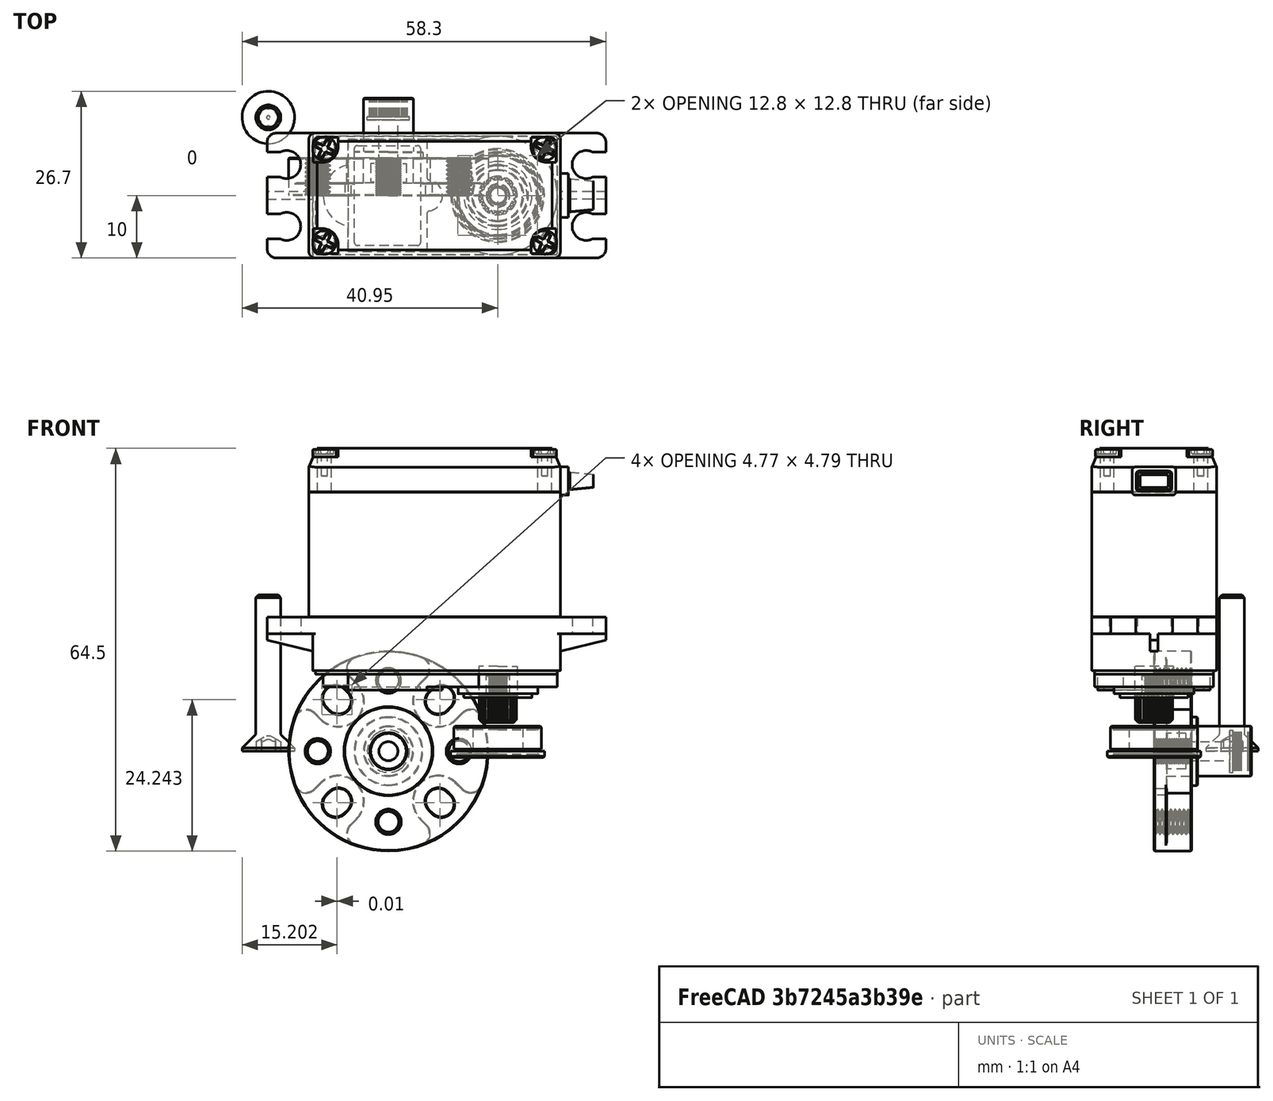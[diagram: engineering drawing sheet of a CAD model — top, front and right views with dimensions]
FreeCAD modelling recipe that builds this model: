
FCSTD DOCUMENT  (FreeCAD 1.1R39747 (Git))
Label: assembly
License: All rights reserved
LicenseURL: https://en.wikipedia.org/wiki/All_rights_reserved
objects: App::Link×11, Part::Feature×3, App::Part×2, App::Point×2, Part::FeaturePython×1, TechDraw::DrawSVGTemplate×1, App::DocumentObjectGroup×1, TechDraw::DrawProjGroupItem×1, TechDraw::DrawPage×1
note: 4 computed .brp shape members not serialized (recipe doc carries the construction recipe); baked Part::Feature solids carry a one-line shape summary decoded from their .brp
EXTERNAL_REF file=claw-base.FCStd obj=Body
EXTERNAL_REF file=claw-back.FCStd obj=Pad
EXTERNAL_REF file=claw-back.FCStd obj=Pad001
EXTERNAL_REF file=claw-back.FCStd obj=Body
EXTERNAL_REF file=variables.FCStd obj=Spreadsheet
EXTERNAL_REF file=claw-pinchers.FCStd obj=InvoluteGear
EXTERNAL_REF file=claw-pinchers.FCStd obj=Body
EXTERNAL_REF file=claw-pinchers.FCStd obj=Body001
EXTERNAL_REF file=DS3225Pro.FCStd obj=DS3225_Pro_Servo_25Kg_4_8_6_8V_H
EXTERNAL_REF file=claw-base.FCStd obj=Sketch001

FEATURE [App::Link] Link  label="Claw Base Body"
  LinkedObject = -> <external claw-base.FCStd>#Body
FEATURE [App::Link] Link001  label="Claw Back Body"
  LinkPlacement = pos=(0,0,-27) rot=(0,0,1;0rad)
  LinkedObject = -> <external claw-back.FCStd>#Body
  Placement = pos=(0,0,-27) rot=(0,0,1;0rad)
  expr: .LinkPlacement.Base.z = -(claw_back#Pad001.Length + claw_back#Pad.Length)
FEATURE [Part::Feature] Part__Feature  label="1611-0514-0008"
  Placement = pos=(17.5,0,4) rot=(1,0,0;-1.5708rad)
  shape: bbox 15 x 15 x 5 mm, 86 faces, 3 solids (baked)
  expr: .Placement.Base.x = variables#Spreadsheet.claw_pincher_c2c / 2
FEATURE [Part::Feature] Part__Feature001  label="1910-0025-0816"
  shape: bbox 32 x 15.92 x 32 mm, 420 faces (baked)
FEATURE [App::Part] _910_0025_0816  label="1910-0025-0817"
  Group = -> [Part__Feature001]
  Origin = -> Origin001
  Placement = pos=(17.5,0,-8) rot=(1,0,0;1.5708rad)
  expr: .Placement.Base.x = variables#Spreadsheet.claw_pincher_c2c / 2
FEATURE [Part::Feature] Part__Feature003  label="2000-0025-0002"
  Placement = pos=(7.7,2.3e-15,10.3) rot=(0,-1,0;3.14159rad)
  shape: bbox 54.3 x 20.57 x 43.9 mm, 516 faces, 2 solids (baked)
  expr: Visibility = variables#Spreadsheet.gobilda_servo_visible
FEATURE [App::Link] Link002  label="1611-0514-0009"
  LinkPlacement = pos=(-17.5,0,4) rot=(1,0,0;-1.5708rad)
  LinkedObject = -> Part__Feature
  Placement = pos=(-17.5,0,4) rot=(1,0,0;-1.5708rad)
  expr: .Placement.Base.x = -<<1611-0514-0008>>.Placement.Base.x
  expr: .Placement.Base.z = <<1611-0514-0008>>.Placement.Base.z
FEATURE [App::Link] Link003  label="1611-0514-0010"
  LinkPlacement = pos=(-17.5,0,-26) rot=(1,0,0;1.5708rad)
  LinkedObject = -> Part__Feature
  Placement = pos=(-17.5,0,-26) rot=(1,0,0;1.5708rad)
  expr: .Placement.Base.x = -<<1611-0514-0011>>.Placement.Base.x
  expr: .Placement.Base.z = <<1611-0514-0011>>.Placement.Base.z
FEATURE [App::Link] Link004  label="1611-0514-0011"
  LinkPlacement = pos=(17.5,0,-26) rot=(1,0,0;1.5708rad)
  LinkedObject = -> Link002
  Placement = pos=(17.5,0,-26) rot=(1,0,0;1.5708rad)
  expr: .Placement.Base.x = <<1611-0514-0008>>.Placement.Base.x
  expr: .Placement.Base.z = Link001.Placement.Base.z + claw_back#Pad.Length - 4 mm
FEATURE [App::Link] Link005  label="Claw Pincher Powered"
  LinkPlacement = pos=(17.5,0,-16.4) rot=(0,0,1;3.14159rad)
  LinkedObject = -> <external claw-pinchers.FCStd>#Body
  Placement = pos=(17.5,0,-16.4) rot=(0,0,1;3.14159rad)
  expr: .Placement.Base.x = variables#Spreadsheet.claw_pincher_c2c / 2
  expr: .Placement.Base.z = -claw_pinchers#InvoluteGear.height - 8 mm
FEATURE [App::Link] Link006  label="Claw Pincher Passive"
  LinkPlacement = pos=(17.5,0,-16.4) rot=(0,0,1;3.14159rad)
  LinkedObject = -> <external claw-pinchers.FCStd>#Body001
  Placement = pos=(17.5,0,-16.4) rot=(0,0,1;3.14159rad)
  expr: .Placement.Base.x = <<Claw Pincher Powered>>.Placement.Base.x
  expr: .Placement.Base.z = <<Claw Pincher Powered>>.Placement.Base.z
FEATURE [App::Link] Link007  label="DS3225 Pro Servo 25Kg 4.8-6.8V H"
  LinkPlacement = pos=(8,-6.6,29.88) rot=(0,-1,0;3.14159rad)
  LinkedObject = -> <external DS3225Pro.FCStd>#DS3225_Pro_Servo_25Kg_4_8_6_8V_H
  Placement = pos=(8,-6.6,29.88) rot=(0,-1,0;3.14159rad)
  expr: Visibility = variables#Spreadsheet.dsservo_visible
FEATURE [Part::FeaturePython] Screw  label="M4x25-Screw"  # WARN: FeaturePython — macro-defined, semantics opaque (R4)
  Diameter = 5
  Invert = false
  LeftHanded = false
  Length = 6
  LengthCustom = 25
  MatchOuter = false
  OffsetAngle = 0
  Placement = pos=(-19.25,12.5,0) rot=(1,0,0;3.14159rad)
  Thread = false
  Type = 54
  expr: .Placement.Base.x = -claw_base#Sketch001.Constraints.structure_hole_x
  expr: .Placement.Base.y = claw_base#Sketch001.Constraints.structure_holes_y
FEATURE [TechDraw::DrawSVGTemplate] Template
  Height = 210
  Orientation = 1
  Template = <path>
  Width = 297
FEATURE [App::Link] Link008  label="M4x8-Screw001"
  LinkPlacement = pos=(-19.25,-12.5,0) rot=(1,0,0;3.14159rad)
  LinkedObject = -> Screw
  Placement = pos=(-19.25,-12.5,0) rot=(1,0,0;3.14159rad)
  expr: .Placement.Base.x = -claw_base#Sketch001.Constraints.structure_hole_x
  expr: .Placement.Base.y = -claw_base#Sketch001.Constraints.structure_holes_y
FEATURE [App::Link] Link009  label="M4x8-Screw002"
  LinkPlacement = pos=(34.25,-12.5,0) rot=(1,0,0;3.14159rad)
  LinkedObject = -> Link008
  Placement = pos=(34.25,-12.5,0) rot=(1,0,0;3.14159rad)
  expr: .Placement.Base.x = -claw_base#Sketch001.Constraints.structure_hole_x + claw_base#Sketch001.Constraints.structure_holes_c2c
  expr: .Placement.Base.y = -claw_base#Sketch001.Constraints.structure_holes_y
FEATURE [App::Link] Link010  label="M4x8-Screw003"
  LinkPlacement = pos=(34.25,12.5,0) rot=(1,0,0;3.14159rad)
  LinkedObject = -> Link009
  Placement = pos=(34.25,12.5,0) rot=(1,0,0;3.14159rad)
  expr: .Placement.Base.x = -claw_base#Sketch001.Constraints.structure_hole_x + claw_base#Sketch001.Constraints.structure_holes_c2c
  expr: .Placement.Base.y = claw_base#Sketch001.Constraints.structure_holes_y
FEATURE [App::Point] Origin002  label="Origin"
  Role = Origin
FEATURE [App::Point] Origin003  label="Origin"
  Role = Origin
FEATURE [App::DocumentObjectGroup] Group  label="AssemblyGroup"
  Group = -> [Link,Link001,Part__Feature,_910_0025_0816,Part__Feature003,Link002,Link004,Link003,Link005,Link006,Link007,Screw,Link008,Link009,Link010]
FEATURE [App::Part] Part  label="Assembly"
  Group = -> [Group,Link,Link001,Part__Feature,_910_0025_0816,Part__Feature003,Link002,Link004,Link003,Link005,Link006,Link007,Screw,Link008,Link009,Link010]
  Origin = -> Origin
  Placement = pos=(0,0,34) rot=(0,0,1;0rad)
FEATURE [TechDraw::DrawProjGroupItem] View
  CoarseView = false
  Direction = (0,0,1)
  Focus = 100
  HardHidden = false
  IsoCount = 0
  IsoHidden = false
  IsoVisible = false
  LockPosition = false
  Perspective = false
  Rotation = 0
  RotationVector = (1,0,0)
  ScaleType = 0
  ScrubCount = 1
  SeamHidden = false
  SeamVisible = false
  SmoothHidden = false
  SmoothVisible = true
  Source = -> [Part]
  Type = 0
  X = 88.6183
  XDirection = (1,0,0)
  Y = 125.531
FEATURE [TechDraw::DrawPage] Page
  KeepUpdated = false
  NextBalloonIndex = 1
  ProjectionType = 0
  Template = -> Template
  Views = -> [View]
note: 1 file-system path scrubbed to <path> (originals preserved in the JSON sidecar)

RESOLVED EXTERNAL PARTS (link-assembly join: the EXTERNAL_REF files above that resolve inside this repo's crawl, each included once):
---- part claw-back.FCStd = doc fcstd_3221efbdef80 ----
FCSTD DOCUMENT  (FreeCAD 1.1R39747 (Git))
Label: claw-back
License: All rights reserved
LicenseURL: https://en.wikipedia.org/wiki/All_rights_reserved
objects: Sketcher::SketchObject×12, PartDesign::Pad×6, PartDesign::Pocket×5, App::Point×2, PartDesign::Hole×1, Part::LocalCoordinateSystem×1, PartDesign::AdditivePipe×1, PartDesign::Body×1
note: 64 computed .brp shape members not serialized (recipe doc carries the construction recipe); baked Part::Feature solids carry a one-line shape summary decoded from their .brp
EXTERNAL_REF file=variables.FCStd obj=Spreadsheet

FEATURE [Sketcher::SketchObject] Sketch
  ArcFitTolerance = 1e-06
  AttachmentSupport = -> [XY_Plane]
  ExternalTypes = [0]
  FullyConstrained = false
  MakeInternals = false
  MapMode = 5
  expr: Constraints[1] = <<variables>>#Spreadsheet.claw_pincher_c2c
  expr: Constraints[30] = <<variables>>#Spreadsheet.claw_back_outer_spacer_holes_wing_angle
  expr: Constraints[33] = <<variables>>#Spreadsheet.claw_back_spacer_diameter / 2
  expr: Constraints[50] = <<variables>>#Spreadsheet.claw_back_outer_spacer_holes_wing_angle
  expr: Constraints[53] = variables#Spreadsheet.distance_bearing_holes_to_end
  sketch-geometry (27):
    g0: LineSegment [constr] StartX=-17.5 StartY=1.14452e-11 StartZ=0 EndX=17.5 EndY=1.14452e-11 EndZ=0
    g1: Circle CenterX=-17.5 CenterY=1.14452e-11 CenterZ=0 NormalX=0 NormalY=0 NormalZ=1 AngleXU=0 Radius=7
    g2: Circle CenterX=17.5 CenterY=1.14452e-11 CenterZ=0 NormalX=0 NormalY=0 NormalZ=1 AngleXU=0 Radius=7
    g3: LineSegment StartX=-27.5 StartY=26.7321 StartZ=0 EndX=-24.5 EndY=28.4641 EndZ=0
    g4: LineSegment StartX=-22.5 StartY=29 StartZ=0 EndX=22.5 EndY=29 EndZ=0
    g5: LineSegment StartX=24.5 StartY=28.4641 StartZ=0 EndX=27.5 EndY=26.7321 EndZ=0
    g6: GeomPoint X=0 Y=29 Z=0
    g7: LineSegment [constr] StartX=-22.5 StartY=25 StartZ=0 EndX=22.5 EndY=25 EndZ=0
    g8: GeomPoint [constr] X=1.28886e-11 Y=25 Z=0
    g9: Circle CenterX=-22.5 CenterY=25 CenterZ=0 NormalX=0 NormalY=0 NormalZ=1 AngleXU=0 Radius=2.25
    g10: Circle CenterX=22.5 CenterY=25 CenterZ=0 NormalX=0 NormalY=0 NormalZ=1 AngleXU=0 Radius=2.25
    g11: Circle [constr] CenterX=-22.5 CenterY=25 CenterZ=0 NormalX=0 NormalY=0 NormalZ=1 AngleXU=0 Radius=4
    g12: Circle [constr] CenterX=22.5 CenterY=25 CenterZ=0 NormalX=0 NormalY=0 NormalZ=1 AngleXU=0 Radius=4
    g13: ArcOfCircle CenterX=22.5 CenterY=25 CenterZ=0 NormalX=0 NormalY=0 NormalZ=1 AngleXU=0 Radius=4 StartAngle=1.0472 EndAngle=1.5708
    g14: ArcOfCircle CenterX=-22.5 CenterY=25 CenterZ=0 NormalX=0 NormalY=0 NormalZ=1 AngleXU=0 Radius=4 StartAngle=1.5708 EndAngle=2.0944
    g15: LineSegment StartX=25 StartY=-16 StartZ=0 EndX=-25 EndY=-16 EndZ=0
    g16: LineSegment StartX=-30 StartY=22.4019 StartZ=0 EndX=-30 EndY=-11 EndZ=0
    g17: ArcOfCircle CenterX=-25 CenterY=-11 CenterZ=0 NormalX=0 NormalY=0 NormalZ=1 AngleXU=0 Radius=5 StartAngle=3.14159 EndAngle=4.71239
    g18: GeomPoint [constr] X=-30 Y=-16 Z=0
    g19: ArcOfCircle CenterX=-25 CenterY=22.4019 CenterZ=0 NormalX=0 NormalY=0 NormalZ=1 AngleXU=0 Radius=5 StartAngle=2.0944 EndAngle=3.14159
    g20: GeomPoint [constr] X=-30 Y=25.2887 Z=0
    g21: ArcOfCircle CenterX=25 CenterY=-11 CenterZ=0 NormalX=0 NormalY=0 NormalZ=1 AngleXU=0 Radius=5 StartAngle=4.71239 EndAngle=6.28319
    g22: GeomPoint [constr] X=30 Y=-16 Z=0
    g23: ArcOfCircle CenterX=25 CenterY=22.4019 CenterZ=0 NormalX=0 NormalY=0 NormalZ=1 AngleXU=0 Radius=5 StartAngle=3.1057e-12 EndAngle=1.0472
    g24: GeomPoint [constr] X=30.2347 Y=25.1532 Z=0
    g25: GeomPoint [constr] X=0 Y=6 Z=0
    g26: LineSegment StartX=30 StartY=22.4019 StartZ=0 EndX=30 EndY=-11 EndZ=0
  constraints (61):
    c: Horizontal(g0)
    c: DistanceX(g0,g0) = 35
    c: Symmetric(g0,g0,g-1)
    c: Diameter(g1) = 14
    c: Coincident(g1,g0)
    c: Coincident(g2,g0)
    c: Equal(g2,g1)
    c: Horizontal(g4)
    c: PointOnObject(g6,g-2)
    c: Horizontal(g7)
    c: DistanceX(g7,g7) = 45
    c: Distance(g0,g7) = 25
    c: Symmetric(g7,g7,g8)
    c: PointOnObject(g8,g-2)
    c: Coincident(g10,g7)
    c: Equal(g9,g10)
    c: Tangent(g4,g11) = 1.5708
    c: Tangent(g3,g11) = 1.5708
    c: Coincident(g12,g7)
    c: Equal(g12,g11)
    c: Equal(g13,g12)
    c: Tangent(g4,g13) = 1.5708
    c: PointOnObject(g6,g4)
    c: Coincident(g5,g13)
    c: Tangent(g5,g12) = 1.5708
    c: Coincident(g14,g3)
    c: Coincident(g14,g4)
    c: Equal(g14,g11)
    c: Diameter(g9) = 4.5
    c: Vertical(g16)
    c: Angle(g3,g7) = 2.61799
    c: Coincident(g9,g14)
    c: Coincident(g7,g11)
    c: Radius(g14) = 4
    c: Horizontal(g15)
    c: PointOnObject(g18,g15)
    c: PointOnObject(g18,g16)
    c: Tangent(g15,g17) = 1.5708
    c: Tangent(g16,g17) = -1.5708
    c: PointOnObject(g20,g3)
    c: PointOnObject(g20,g16)
    c: Tangent(g3,g19) = 1.5708
    c: Tangent(g16,g19) = -1.5708
    c: Radius(g17) = 5
    c: Equal(g19,g17)
    c: Tangent(g26,g21) = 1.5708
    c: Equal(g21,g17)
    c: PointOnObject(g24,g5)
    c: Tangent(g5,g23) = 1.5708
    c: Equal(g23,g21)
    c: Angle(g7,g5) = 2.61799
    c: Horizontal(g22,g15)
    c: Equal(g3,g5)
    c: Distance(g15,g0) = 16
    c: Tangent(g21,g15) = 1.5708
    c: PointOnObject(g25,g-2)
    c: Distance(g25,g0) = 6
    c: Vertical(g26)
    c: PointOnObject(g22,g26)
    c: Tangent(g26,g23) = 1.5708
    c: Distance(g26,g16) = 60
FEATURE [PartDesign::Pad] Pad
  Direction = (0,0,1)
  Length = 5
  Length2 = 10
  Profile = -> Sketch
  ReferenceAxis = -> Sketch [N_Axis]
  Refine = true
  Suppressed = false
  Type = 0
FEATURE [Sketcher::SketchObject] Sketch001
  ArcFitTolerance = 1e-06
  AttachmentSupport = -> [Pad]
  ExternalGeometry = -> [Pad]
  ExternalTypes = [0]
  FullyConstrained = true
  MakeInternals = false
  MapMode = 5
  Placement = pos=(0,0,5) rot=(0,0,1;0rad)
  expr: Constraints[12] = <<variables>>#Spreadsheet.claw_back_spacer_diameter / 2
  sketch-geometry (6):
    g0: ArcOfCircle CenterX=22.5 CenterY=25 CenterZ=0 NormalX=0 NormalY=0 NormalZ=1 AngleXU=0 Radius=4 StartAngle=4.71239 EndAngle=7.85398
    g1: Circle CenterX=22.5 CenterY=25 CenterZ=0 NormalX=0 NormalY=0 NormalZ=1 AngleXU=0 Radius=2.25
    g2: ArcOfCircle CenterX=-22.5 CenterY=25 CenterZ=0 NormalX=0 NormalY=0 NormalZ=1 AngleXU=0 Radius=4 StartAngle=1.5708 EndAngle=4.71239
    g3: LineSegment StartX=-22.5 StartY=29 StartZ=0 EndX=22.5 EndY=29 EndZ=0
    g4: LineSegment StartX=22.5 StartY=21 StartZ=0 EndX=-22.5 EndY=21 EndZ=0
    g5: Circle CenterX=-22.5 CenterY=25 CenterZ=0 NormalX=0 NormalY=0 NormalZ=1 AngleXU=0 Radius=2.25
  constraints (13):
    c: Coincident(g0,g-3)
    c: Coincident(g1,g0)
    c: Equal(g-3,g1)
    c: Coincident(g2,g-4)
    c: Horizontal(g3)
    c: Horizontal(g4)
    c: Tangent(g3,g0) = 1.5708
    c: Tangent(g2,g3) = 1.5708
    c: Coincident(g5,g2)
    c: Equal(g-4,g5)
    c: Coincident(g0,g4)
    c: Tangent(g4,g2) = 1.5708
    c: Radius(g2) = 4
FEATURE [PartDesign::Pad] Pad001
  BaseFeature = -> Pad
  Direction = (0,0,1)
  Length = 22
  Length2 = 10
  Profile = -> Sketch001
  ReferenceAxis = -> Sketch001 [N_Axis]
  Refine = true
  Suppressed = false
  Type = 0
  expr: Length = variables#Spreadsheet.claw_back_spacer_length
FEATURE [Sketcher::SketchObject] Sketch002
  ArcFitTolerance = 1e-06
  AttachmentSupport = -> [Pad001]
  ExternalGeometry = -> [Pad001]
  ExternalTypes = [0]
  FullyConstrained = true
  MakeInternals = false
  MapMode = 5
  Placement = pos=(2.268e-13,29,3.4653e-11) rot=(0,0.707107,0.707107;3.14159rad)
  expr: Constraints[14] = <<variables>>#Spreadsheet.claw_base_thickness
  sketch-geometry (7):
    g0: LineSegment [constr] StartX=-25 StartY=35.7 StartZ=0 EndX=25 EndY=35.7 EndZ=0
    g1: GeomPoint [constr] X=0 Y=35.7 Z=0
    g2: LineSegment [constr] StartX=-11.3137 StartY=17.85 StartZ=0 EndX=11.3137 EndY=17.85 EndZ=0
    g3: GeomPoint [constr] X=0 Y=17.85 Z=0
    g4: Circle CenterX=-11.3137 CenterY=17.85 CenterZ=0 NormalX=0 NormalY=0 NormalZ=1 AngleXU=0 Radius=2.25
    g5: Circle CenterX=11.3137 CenterY=17.85 CenterZ=0 NormalX=0 NormalY=0 NormalZ=1 AngleXU=0 Radius=2.25
    g6: Circle CenterX=0 CenterY=17.85 CenterZ=0 NormalX=0 NormalY=0 NormalZ=1 AngleXU=0 Radius=5
  constraints (15):
    c: Distance(g0) = 50
    c: Horizontal(g0)
    c: Symmetric(g0,g0,g1)
    c: PointOnObject(g1,g-2)
    c: Horizontal(g2)
    c: DistanceX(g2,g2) = 22.6274
    c: Symmetric(g2,g2,g3)
    c: Symmetric(g1,g-1,g3)
    c: Diameter(g4) = 4.5
    c: Coincident(g4,g2)
    c: Coincident(g5,g2)
    c: Equal(g4,g5)
    c: Diameter(g6) = 10
    c: Coincident(g6,g3)
    c: Distance(g0,g-3) = 8.7
FEATURE [PartDesign::Pocket] Pocket
  BaseFeature = -> Pad001
  Direction = (-7.8e-15,-1,-1.195e-12)
  Length = 0
  Length2 = 5
  Profile = -> Sketch002
  ReferenceAxis = -> Sketch002 [N_Axis]
  Refine = true
  Suppressed = true
  Type = 3
  UpToFace = -> Pad001 [Face14]
  expr: Suppressed = variables#Spreadsheet.rex_mount
FEATURE [Sketcher::SketchObject] Sketch003
  ArcFitTolerance = 1e-06
  AttachmentSupport = -> [Pocket]
  ExternalTypes = [0]
  FullyConstrained = true
  MakeInternals = false
  MapMode = 5
  Placement = pos=(0,21,0) rot=(1,0,0;1.5708rad)
  sketch-geometry (2):
    g0: Circle CenterX=-11.3137 CenterY=17.85 CenterZ=0 NormalX=0 NormalY=0 NormalZ=1 AngleXU=0 Radius=4.75
    g1: Circle CenterX=11.3137 CenterY=17.85 CenterZ=0 NormalX=0 NormalY=0 NormalZ=1 AngleXU=0 Radius=4.75
  constraints (4):
    c: Diameter(g0) = 9.5
    c: Equal(g1,g0)
    c: Coincident(g-4,g1)
    c: Coincident(g-3,g0)
FEATURE [PartDesign::Pocket] Pocket001
  BaseFeature = -> Pocket
  Direction = (0,1,-2e-16)
  Length = 0
  Length2 = 5
  Offset = 2
  Profile = -> Sketch003
  ReferenceAxis = -> Sketch003 [N_Axis]
  Refine = true
  Suppressed = true
  Type = 3
  UpToFace = -> Pocket [Face16]
  expr: Suppressed = variables#Spreadsheet.rex_mount + variables#Spreadsheet.Hub_Mount_Countersink
FEATURE [Sketcher::SketchObject] Sketch004
  ArcFitTolerance = 1e-06
  AttachmentSupport = -> [Pocket001]
  ExternalGeometry = -> [Pocket001]
  ExternalTypes = [0]
  FullyConstrained = true
  MakeInternals = false
  MapMode = 5
  Placement = pos=(2.268e-13,29,3.4653e-11) rot=(0,0.707107,0.707107;3.14159rad)
  expr: Constraints[4] = <<variables>>#Spreadsheet.claw_base_thickness
  sketch-geometry (14):
    g0: LineSegment [constr] StartX=-25 StartY=35.7 StartZ=0 EndX=25 EndY=35.7 EndZ=0
    g1: GeomPoint [constr] X=-1.056e-13 Y=35.7 Z=0
    g2: ArcOfCircle CenterX=-2.462e-13 CenterY=17.85 CenterZ=0 NormalX=0 NormalY=0 NormalZ=1 AngleXU=0 Radius=17.5 StartAngle=2.80317 EndAngle=6.62161
    g3: LineSegment StartX=-11.791 StartY=27 StartZ=0 EndX=11.791 EndY=27 EndZ=0
    g4: LineSegment StartX=3.575 StartY=19.914 StartZ=0 EndX=-2.669e-13 EndY=21.9781 EndZ=0
    g5: LineSegment StartX=-2.669e-13 StartY=21.9781 StartZ=0 EndX=-3.575 EndY=19.914 EndZ=0
    g6: LineSegment StartX=-3.575 StartY=19.914 StartZ=0 EndX=-3.575 EndY=15.786 EndZ=0
    g7: LineSegment StartX=-3.575 StartY=15.786 StartZ=0 EndX=-3.353e-13 EndY=13.7219 EndZ=0
    g8: LineSegment StartX=-3.353e-13 StartY=13.7219 StartZ=0 EndX=3.575 EndY=15.786 EndZ=0
    g9: LineSegment StartX=3.575 StartY=15.786 StartZ=0 EndX=3.575 EndY=19.914 EndZ=0
    g10: Circle [constr] CenterX=-2.462e-13 CenterY=17.85 CenterZ=0 NormalX=0 NormalY=0 NormalZ=1 AngleXU=0 Radius=4.12805
    g11: Circle [constr] CenterX=-2.462e-13 CenterY=17.85 CenterZ=0 NormalX=0 NormalY=0 NormalZ=1 AngleXU=0 Radius=3.575
    g12: ArcOfCircle CenterX=11.791 CenterY=22 CenterZ=0 NormalX=0 NormalY=0 NormalZ=1 AngleXU=0 Radius=5 StartAngle=0.338423 EndAngle=1.5708
    g13: ArcOfCircle CenterX=-11.791 CenterY=22 CenterZ=0 NormalX=0 NormalY=0 NormalZ=1 AngleXU=0 Radius=5 StartAngle=1.5708 EndAngle=2.80317
  constraints (34):
    c: Distance(g0) = 50
    c: Horizontal(g0)
    c: Symmetric(g0,g0,g1)
    c: PointOnObject(g1,g-2)
    c: Distance(g1,g-3) = 8.7
    c: Diameter(g2) = 35
    c: Symmetric(g-1,g1,g2)
    c: Horizontal(g3)
    c: Coincident(g4,g5)
    c: Coincident(g5,g6)
    c: Coincident(g6,g7)
    c: Coincident(g7,g8)
    c: Coincident(g8,g9)
    c: Coincident(g9,g4)
    c: Equal(g4, g5-g9) x5
    c: PointOnObject(g4,g10)
    c: PointOnObject(g5,g10)
    c: PointOnObject(g6,g10)
    c: PointOnObject(g7,g10)
    c: PointOnObject(g8,g10)
    c: PointOnObject(g9,g10)
    c: Coincident(g10,g2)
    c: Vertical(g9)
    c: Coincident(g11,g2)
    c: Tangent(g11,g4)
    c: Diameter(g11) = 7.15  'rex_thickness'
    c: Tangent(g2,g12) = -1.5708
    c: Tangent(g3,g12) = 1.5708
    c: Tangent(g2,g13) = -1.5708
    c: Tangent(g3,g13) = 1.5708
    c: Radius(g13) = 5
    c: Equal(g12,g13)
    c: PointOnObject(g3,g-3)
    c: Distance(g2,g-3) = 9.15  'MountDistFromWall'
FEATURE [App::Point] Origin001  label="Origin"
  Role = Origin
FEATURE [App::Point] Origin002
  Role = Origin
FEATURE [PartDesign::Hole] Hole
  BaseFeature = -> Pocket001
  CustomThreadClearance = 0
  Depth = 25
  DepthType = 0
  Diameter = 4.5
  DrillForDepth = false
  DrillPoint = 1
  DrillPointAngle = 118
  HoleCutCountersinkAngle = 90
  HoleCutCustomValues = false
  HoleCutDepth = 3
  HoleCutDiameter = 9
  HoleCutType = 2
  ModelThread = false
  Profile = -> Pocket001 [?Edge42,?Edge40]
  Refine = true
  Reversed = true
  Suppressed = true
  Tapered = false
  TaperedAngle = 90
  ThreadClass = 0
  ThreadDepth = 25
  ThreadDepthType = 0
  ThreadDirection = 0
  ThreadFit = 0
  ThreadSize = 11
  ThreadType = 1
  Threaded = false
  UseCustomThreadClearance = false
  expr: Suppressed = 2 - (variables#Spreadsheet.hub_mount + variables#Spreadsheet.Hub_Mount_Countersink)
FEATURE [PartDesign::Pad] Pad002
  BaseFeature = -> Hole
  Direction = (7.8e-15,1,1.195e-12)
  Length = 3
  Length2 = 10
  Profile = -> Sketch004
  ReferenceAxis = -> Sketch004 [N_Axis]
  Refine = true
  Suppressed = false
  Type = 0
  expr: Suppressed = variables#Spreadsheet.hub_mount
FEATURE [Sketcher::SketchObject] Sketch005
  ArcFitTolerance = 1e-06
  AttachmentSupport = -> [Pad002]
  ExternalGeometry = -> [Pad002]
  ExternalTypes = [0]
  FullyConstrained = true
  MakeInternals = false
  MapMode = 5
  Placement = pos=(2.268e-13,29,3.4653e-11) rot=(0,0.707107,0.707107;3.14159rad)
  expr: Constraints[20] = Sketch004.Constraints.rex_thickness
  sketch-geometry (8):
    g0: LineSegment StartX=3.575 StartY=19.914 StartZ=0 EndX=4.3108e-12 EndY=21.9781 EndZ=0
    g1: LineSegment StartX=4.3108e-12 StartY=21.9781 StartZ=0 EndX=-3.575 EndY=19.914 EndZ=0
    g2: LineSegment StartX=-3.575 StartY=19.914 StartZ=0 EndX=-3.575 EndY=15.786 EndZ=0
    g3: LineSegment StartX=-3.575 StartY=15.786 StartZ=0 EndX=-4.1283e-12 EndY=13.7219 EndZ=0
    g4: LineSegment StartX=-4.1283e-12 StartY=13.7219 StartZ=0 EndX=3.575 EndY=15.786 EndZ=0
    g5: LineSegment StartX=3.575 StartY=15.786 StartZ=0 EndX=3.575 EndY=19.914 EndZ=0
    g6: Circle [constr] CenterX=-2.462e-13 CenterY=17.85 CenterZ=0 NormalX=0 NormalY=0 NormalZ=1 AngleXU=0 Radius=4.12805
    g7: Circle [constr] CenterX=-2.462e-13 CenterY=17.85 CenterZ=0 NormalX=0 NormalY=0 NormalZ=1 AngleXU=0 Radius=3.575
  constraints (18):
    c: Coincident(g0,g1)
    c: Coincident(g1,g2)
    c: Coincident(g2,g3)
    c: Coincident(g3,g4)
    c: Coincident(g4,g5)
    c: Coincident(g5,g0)
    c: Equal(g0, g1-g5) x5
    c: PointOnObject(g0,g6)
    c: PointOnObject(g1,g6)
    c: PointOnObject(g2,g6)
    c: PointOnObject(g3,g6)
    c: PointOnObject(g4,g6)
    c: PointOnObject(g5,g6)
    c: Coincident(g6,g-3)
    c: Coincident(g7,g6)
    c: Tangent(g7,g5)
    c: Diameter(g7) = 7.15
    c: Vertical(g5)
FEATURE [PartDesign::Pocket] Pocket002
  BaseFeature = -> Pad002
  Direction = (-7.8e-15,-1,-1.195e-12)
  Length = 0
  Length2 = 5
  Profile = -> Sketch005
  ReferenceAxis = -> Sketch005 [N_Axis]
  Refine = true
  Suppressed = false
  Type = 3
  UpToFace = -> Pad002 [Face7]
  expr: Suppressed = variables#Spreadsheet.hub_mount
FEATURE [Sketcher::SketchObject] Sketch006
  ArcFitTolerance = 1e-06
  AttachmentSupport = -> [Pocket002]
  ExternalGeometry = -> [Pocket002]
  ExternalTypes = [0,0,0,0,0,0]
  FullyConstrained = true
  MakeInternals = false
  MapMode = 5
  Placement = pos=(0,21,0) rot=(1,0,0;1.5708rad)
  sketch-geometry (2):
    g0: Circle [constr] CenterX=7.888e-13 CenterY=17.85 CenterZ=0 NormalX=0 NormalY=0 NormalZ=1 AngleXU=0 Radius=3.575
    g1: Circle CenterX=7.888e-13 CenterY=17.85 CenterZ=0 NormalX=0 NormalY=0 NormalZ=1 AngleXU=0 Radius=6
  constraints (5):
    c: Tangent(g0,g-8)
    c: Tangent(g0,g-5)
    c: Tangent(g0,g-6)
    c: Coincident(g1,g0)
    c: Diameter(g1) = 12
FEATURE [PartDesign::Pad] Pad003
  BaseFeature = -> Pocket002
  Direction = (0,-1,2e-16)
  Length = 2
  Length2 = 10
  Profile = -> Sketch006
  ReferenceAxis = -> Sketch006 [N_Axis]
  Refine = true
  Suppressed = false
  Type = 0
  expr: Suppressed = variables#Spreadsheet.hub_mount
FEATURE [Sketcher::SketchObject] Sketch007
  ArcFitTolerance = 1e-06
  AttachmentOffset = pos=(0,0,2) rot=(0,0,1;0rad)
  AttachmentSupport = -> [Pad003]
  ExternalTypes = [0]
  FullyConstrained = true
  MakeInternals = false
  MapMode = 5
  Placement = pos=(0,19,4e-16) rot=(1,0,0;1.5708rad)
  expr: .AttachmentOffset.Base.z = Pad003.Length
  sketch-geometry (1):
    g0: Circle CenterX=0 CenterY=17.85 CenterZ=0 NormalX=0 NormalY=0 NormalZ=1 AngleXU=0 Radius=2.25
  constraints (2):
    c: Diameter(g0) = 4.5
    c: Coincident(g0,g-3)
FEATURE [PartDesign::Pad] Pad004
  BaseFeature = -> Pad003
  Direction = (0,-1,2e-16)
  Length = 1.5
  Length2 = 10
  Profile = -> Sketch007
  ReferenceAxis = -> Sketch007 [N_Axis]
  Refine = true
  Suppressed = false
  Type = 0
  expr: Suppressed = variables#Spreadsheet.hub_mount
FEATURE [Part::LocalCoordinateSystem] LCS
  AttacherType = Attacher::AttachEngine3D
  AttachmentOffset = pos=(-3.5,-9.15,0) rot=(0,-1,0;1.5708rad)
  AttachmentSupport = -> [Pad004]
  MapMode = 45
  OriginFeatures = -> [X_Axis001,Y_Axis001,Z_Axis001,XY_Plane001,XZ_Plane001,YZ_Plane001,Origin002]
  Placement = pos=(-1.2125e-08,17.5,17.85) rot=(1,0,0;1.5708rad)
  expr: .AttachmentOffset.Base.x = -(Pad003.Length + Pad004.Length)
  expr: .AttachmentOffset.Base.y = -Sketch004.Constraints.MountDistFromWall
  expr: .AttachmentOffset.Base.z = 0
FEATURE [Sketcher::SketchObject] Sketch008
  ArcFitTolerance = 1e-06
  AttachmentSupport = -> [YZ_Plane001]
  ExternalGeometry = -> [Pad004]
  ExternalTypes = [0,0]
  FullyConstrained = true
  MakeInternals = false
  MapMode = 5
  Placement = pos=(0,0,0) rot=(0.57735,0.57735,0.57735;2.0944rad)
  sketch-geometry (3):
    g0: LineSegment StartX=17.5 StartY=23.85 StartZ=0 EndX=21 EndY=23.85 EndZ=0
    g1: LineSegment StartX=21 StartY=23.85 StartZ=0 EndX=21 EndY=27 EndZ=0
    g2: ArcOfCircle CenterX=17.8325 CenterY=27 CenterZ=0 NormalX=0 NormalY=0 NormalZ=1 AngleXU=0 Radius=3.1675 StartAngle=4.60722 EndAngle=6.28319
  constraints (7):
    c: PointOnObject(g0,g-3)
    c: Horizontal(g0)
    c: Coincident(g1,g0)
    c: Coincident(g1,g-3)
    c: Coincident(g2,g0)
    c: Tangent(g2,g1) = -1.5708
    c: Coincident(g-4,g0)
FEATURE [PartDesign::AdditivePipe] AdditivePipe
  AuxilleryCurvelinear = true
  AuxillerySpineTangent = false
  BaseFeature = -> Pad004
  Binormal = (0,0,0)
  Mode = 0
  Profile = -> Sketch008
  Refine = true
  Spine = -> Pad004 [Edge40]
  SpineTangent = false
  Suppressed = false
  Transformation = 0
  Transition = 0
  expr: Suppressed = variables#Spreadsheet.hub_mount
FEATURE [Sketcher::SketchObject] Sketch009
  ArcFitTolerance = 1e-06
  AttachmentSupport = -> [AdditivePipe]
  ExternalGeometry = -> [AdditivePipe]
  ExternalTypes = [0,0,0]
  FullyConstrained = true
  MakeInternals = false
  MapMode = 5
  Placement = pos=(0,0,0) rot=(1,0,0;3.14159rad)
  sketch-geometry (13):
    g0: LineSegment [constr] StartX=-29.5 StartY=-13.5 StartZ=0 EndX=29.5 EndY=-13.5 EndZ=0
    g1: LineSegment [constr] StartX=29.5 StartY=-13.5 StartZ=0 EndX=29.5 EndY=-3.5 EndZ=0
    g2: LineSegment [constr] StartX=29.5 StartY=-3.5 StartZ=0 EndX=-29.5 EndY=-3.5 EndZ=0
    g3: LineSegment [constr] StartX=-29.5 StartY=-3.5 StartZ=0 EndX=-29.5 EndY=-13.5 EndZ=0
    g4: GeomPoint [constr] X=0 Y=-8.5 Z=0
    g5: ArcOfCircle CenterX=29.5 CenterY=-3.5 CenterZ=0 NormalX=0 NormalY=0 NormalZ=1 AngleXU=0 Radius=4.5 StartAngle=6.13426e-06 EndAngle=1.45946
    g6: LineSegment StartX=34 StartY=-13.5 StartZ=0 EndX=34 EndY=-3.49997 EndZ=0
    g7: ArcOfCircle CenterX=29.5 CenterY=-13.5 CenterZ=0 NormalX=0 NormalY=0 NormalZ=1 AngleXU=0 Radius=4.5 StartAngle=4.82373 EndAngle=6.28319
    g8: ArcOfCircle CenterX=-29.5 CenterY=-3.5 CenterZ=0 NormalX=0 NormalY=0 NormalZ=1 AngleXU=0 Radius=4.5 StartAngle=1.68214 EndAngle=3.14159
    g9: ArcOfCircle CenterX=-29.5 CenterY=-13.5 CenterZ=0 NormalX=0 NormalY=0 NormalZ=1 AngleXU=0 Radius=4.5 StartAngle=3.14159 EndAngle=4.60105
    g10: LineSegment StartX=-34 StartY=-13.5 StartZ=0 EndX=-34 EndY=-3.5 EndZ=0
    g11: LineSegment StartX=-30 StartY=-17.9721 StartZ=0 EndX=-30 EndY=0.972136 EndZ=0
    g12: LineSegment StartX=30 StartY=-17.9721 StartZ=0 EndX=30 EndY=0.972136 EndZ=0
  constraints (36):
    c: Coincident(g0,g1)
    c: Coincident(g1,g2)
    c: Coincident(g2,g3)
    c: Coincident(g3,g0)
    c: Horizontal(g0)
    c: Horizontal(g2)
    c: Vertical(g1)
    c: Vertical(g3)
    c: Symmetric(g2,g0,g4)
    c: Distance(g1,g3) = 59
    c: Distance(g0,g2) = 10
    c: Coincident(g5,g1)
    c: Vertical(g6)
    c: Tangent(g6,g7) = -1.5708
    c: Coincident(g6,g5)
    c: Diameter(g5) = 9
    c: Equal(g7,g5)
    c: Coincident(g7,g0)
    c: Coincident(g8,g2)
    c: Horizontal(g2,g8)
    c: Equal(g8,g5)
    c: Coincident(g9,g0)
    c: Horizontal(g0,g9)
    c: Equal(g9,g8)
    c: Coincident(g10,g8)
    c: Coincident(g9,g10)
    c: PointOnObject(g8,g-5)
    c: PointOnObject(g9,g-5)
    c: Coincident(g11,g9)
    c: Coincident(g11,g8)
    c: PointOnObject(g5,g-4)
    c: PointOnObject(g7,g-4)
    c: Coincident(g12,g7)
    c: Coincident(g12,g5)
    c: PointOnObject(g4,g-2)
    c: DistanceY(g4,g-1) = 8.5
FEATURE [PartDesign::Pad] Pad005
  BaseFeature = -> AdditivePipe
  Direction = (0,0,-1)
  Length = 10
  Length2 = 10
  Profile = -> Sketch009
  ReferenceAxis = -> Sketch009 [N_Axis]
  Refine = true
  Suppressed = true
  Type = 3
  UpToFace = -> AdditivePipe [Face5]
  expr: Suppressed = -(variables#Spreadsheet.use_camera_mount - 1)
FEATURE [Sketcher::SketchObject] Sketch010
  ArcFitTolerance = 1e-06
  AttachmentSupport = -> [Pad005]
  ExternalGeometry = -> [Pad005]
  ExternalTypes = [0,0,0,0,0]
  FullyConstrained = true
  MakeInternals = false
  MapMode = 11
  Placement = pos=(17.5,1.14452e-11,5) rot=(0,0,1;1.5708rad)
  sketch-geometry (4):
    g0: Circle CenterX=13.5 CenterY=-12 CenterZ=0 NormalX=0 NormalY=0 NormalZ=1 AngleXU=0 Radius=2.25
    g1: Circle CenterX=3.5 CenterY=-12 CenterZ=0 NormalX=0 NormalY=0 NormalZ=1 AngleXU=0 Radius=2.25
    g2: Circle CenterX=3.5 CenterY=47 CenterZ=0 NormalX=0 NormalY=0 NormalZ=1 AngleXU=0 Radius=2.25
    g3: Circle CenterX=13.5 CenterY=47 CenterZ=0 NormalX=0 NormalY=0 NormalZ=1 AngleXU=0 Radius=2.25
  constraints (8):
    c: Coincident(g0,g-5)
    c: Coincident(g1,g-6)
    c: Coincident(g2,g-4)
    c: Coincident(g3,g-3)
    c: Equal(g2,g3)
    c: Equal(g3,g0)
    c: Equal(g0,g1)
    c: Equal(g1,g-7)
FEATURE [PartDesign::Pocket] Pocket003
  BaseFeature = -> Pad005
  Direction = (0,0,-1)
  Length = 0
  Length2 = 5
  Profile = -> Sketch010
  ReferenceAxis = -> Sketch010 [N_Axis]
  Refine = true
  Suppressed = true
  Type = 3
  UpToFace = -> Pad005 [?Face32]
  expr: Suppressed = -(variables#Spreadsheet.use_camera_mount - 1)
FEATURE [Sketcher::SketchObject] Sketch011
  ArcFitTolerance = 1e-06
  AttachmentSupport = -> [Pocket003]
  ExternalGeometry = -> [Pocket003]
  ExternalTypes = [0]
  FullyConstrained = true
  MakeInternals = false
  MapMode = 11
  Placement = pos=(-17.5,1.14452e-11,0) rot=(0,0,1;1.5708rad)
  sketch-geometry (5):
    g0: GeomPoint X=29 Y=-17.5 Z=0
    g1: LineSegment StartX=23 StartY=-17.5 StartZ=0 EndX=35 EndY=-17.5 EndZ=0
    g2: LineSegment StartX=35 StartY=-17.5 StartZ=0 EndX=35 EndY=-10.5 EndZ=0
    g3: LineSegment StartX=35 StartY=-10.5 StartZ=0 EndX=23 EndY=-10.5 EndZ=0
    g4: LineSegment StartX=23 StartY=-10.5 StartZ=0 EndX=23 EndY=-17.5 EndZ=0
  constraints (12):
    c: Symmetric(g-3,g-3,g0)
    c: Coincident(g1,g2)
    c: Coincident(g2,g3)
    c: Coincident(g3,g4)
    c: Coincident(g4,g1)
    c: Horizontal(g1)
    c: Horizontal(g3)
    c: Vertical(g2)
    c: Vertical(g4)
    c: Symmetric(g1,g1,g0)
    c: DistanceX(g3,g3) = 12
    c: DistanceY(g2,g2) = 7
FEATURE [PartDesign::Pocket] Pocket004
  BaseFeature = -> Pocket003
  Direction = (0,0,-1)
  Length = 7
  Length2 = 5
  Profile = -> Sketch011
  ReferenceAxis = -> Sketch011 [N_Axis]
  Refine = true
  Suppressed = true
  Type = 0
  expr: Suppressed = -(variables#Spreadsheet.use_camera_mount - 1)
FEATURE [PartDesign::Body] Body  label="Claw Back Body"
  AllowCompound = false
  Group = -> [Sketch,Pad,Sketch001,Pad001,Sketch002,Pocket,Sketch003,Pocket001,Sketch004,Hole,Pad002,Sketch005,Pocket002,Sketch006,Pad003,Sketch007,Pad004,LCS,Sketch008,AdditivePipe,Sketch009,Pad005,Sketch010,Pocket003,Sketch011,Pocket004]
  Origin = -> Origin
  Tip = -> Pocket004
---- part claw-base.FCStd = doc fcstd_766c7846706b ----
FCSTD DOCUMENT  (FreeCAD 1.1R39741 (Git))
Label: claw-base
License: All rights reserved
LicenseURL: https://en.wikipedia.org/wiki/All_rights_reserved
objects: Part::Feature×5, Sketcher::SketchObject×4, PartDesign::Pocket×4, PartDesign::Pad×2, PartDesign::Mirrored×2, PartDesign::CoordinateSystem×1, Part::Compound×1, Part::Scale×1, PartDesign::Hole×1, PartDesign::Plane×1, PartDesign::Body×1, App::Point×1
note: 43 computed .brp shape members not serialized (recipe doc carries the construction recipe); baked Part::Feature solids carry a one-line shape summary decoded from their .brp
EXTERNAL_REF file=variables.FCStd obj=Spreadsheet

FEATURE [Sketcher::SketchObject] Sketch
  ArcFitTolerance = 1e-06
  ExternalTypes = [0]
  FullyConstrained = true
  MakeInternals = false
  MapMode = 5
  expr: Constraints[29] = variables#Spreadsheet.distance_bearing_holes_to_end
  expr: Constraints[35] = variables#Spreadsheet.claw_back_spacer_diameter
  expr: Constraints[36] = <<variables>>#Spreadsheet.claw_back_outer_spacer_holes_wing_angle
  expr: Constraints[4] = <<variables>>#Spreadsheet.claw_pincher_c2c
  expr: Constraints[52] = <<variables>>#Spreadsheet.claw_back_outer_spacer_holes_wing_angle
  sketch-geometry (25):
    g0: LineSegment StartX=41 StartY=-11 StartZ=0 EndX=41 EndY=16.6284 EndZ=0
    g1: GeomPoint X=41 Y=-16 Z=0
    g2: LineSegment [constr] StartX=-17.5 StartY=5.631e-13 StartZ=0 EndX=17.5 EndY=5.631e-13 EndZ=0
    g3: Circle CenterX=-17.5 CenterY=5.631e-13 CenterZ=0 NormalX=0 NormalY=0 NormalZ=1 AngleXU=0 Radius=7
    g4: Circle CenterX=17.5 CenterY=5.631e-13 CenterZ=0 NormalX=0 NormalY=0 NormalZ=1 AngleXU=0 Radius=7
    g5: LineSegment StartX=-39 StartY=20.0925 StartZ=0 EndX=-24.5 EndY=28.4641 EndZ=0
    g6: LineSegment StartX=-22.5 StartY=29 StartZ=0 EndX=22.5 EndY=29 EndZ=0
    g7: LineSegment StartX=24.5 StartY=28.4641 StartZ=0 EndX=39 EndY=20.0925 EndZ=0
    g8: LineSegment [constr] StartX=-22.5 StartY=25 StartZ=0 EndX=22.5 EndY=25 EndZ=0
    g9: GeomPoint [constr] X=-1.358e-13 Y=25 Z=0
    g10: Circle CenterX=-22.5 CenterY=25 CenterZ=0 NormalX=0 NormalY=0 NormalZ=1 AngleXU=0 Radius=2.25
    g11: Circle CenterX=22.5 CenterY=25 CenterZ=0 NormalX=0 NormalY=0 NormalZ=1 AngleXU=0 Radius=2.25
    g12: Circle [constr] CenterX=-22.5 CenterY=25 CenterZ=0 NormalX=0 NormalY=0 NormalZ=1 AngleXU=0 Radius=4
    g13: Circle [constr] CenterX=22.5 CenterY=25 CenterZ=0 NormalX=0 NormalY=0 NormalZ=1 AngleXU=0 Radius=4
    g14: ArcOfCircle CenterX=22.5 CenterY=25 CenterZ=0 NormalX=0 NormalY=0 NormalZ=1 AngleXU=0 Radius=4 StartAngle=1.0472 EndAngle=1.5708
    g15: ArcOfCircle CenterX=37 CenterY=16.6284 CenterZ=0 NormalX=0 NormalY=0 NormalZ=1 AngleXU=0 Radius=4 StartAngle=2.005e-13 EndAngle=1.0472
    g16: ArcOfCircle CenterX=-22.5 CenterY=25 CenterZ=0 NormalX=0 NormalY=0 NormalZ=1 AngleXU=0 Radius=4 StartAngle=1.5708 EndAngle=2.0944
    g17: LineSegment StartX=36 StartY=-16 StartZ=0 EndX=-36 EndY=-16 EndZ=0
    g18: LineSegment StartX=-41 StartY=16.6284 StartZ=0 EndX=-41 EndY=-11 EndZ=0
    g19: ArcOfCircle CenterX=-36 CenterY=-11 CenterZ=0 NormalX=0 NormalY=0 NormalZ=1 AngleXU=0 Radius=5 StartAngle=3.14159 EndAngle=4.71239
    g20: GeomPoint [constr] X=-41 Y=-16 Z=0
    g21: ArcOfCircle CenterX=36 CenterY=-11 CenterZ=0 NormalX=0 NormalY=0 NormalZ=1 AngleXU=0 Radius=5 StartAngle=4.71239 EndAngle=6.28319
    g22: GeomPoint [constr] X=41 Y=-16 Z=0
    g23: ArcOfCircle CenterX=-37 CenterY=16.6284 CenterZ=0 NormalX=0 NormalY=0 NormalZ=1 AngleXU=0 Radius=4 StartAngle=2.0944 EndAngle=3.14159
    g24: GeomPoint [constr] X=-41 Y=18.9378 Z=0
  constraints (58):
    c: Vertical(g0)
    c: Vertical(g22,g1)
    c: Horizontal(g22,g1)
    c: Horizontal(g2)
    c: DistanceX(g2,g2) = 35
    c: Symmetric(g2,g2,g-1)
    c: Diameter(g3) = 14
    c: Coincident(g3,g2)
    c: Coincident(g4,g2)
    c: Equal(g4,g3)
    c: Horizontal(g6)
    c: Horizontal(g8)
    c: DistanceX(g8,g8) = 45
    c: Distance(g2,g8) = 25
    c: Symmetric(g8,g8,g9)
    c: PointOnObject(g9,g-2)
    c: Coincident(g11,g8)
    c: Equal(g10,g11)
    c: Tangent(g6,g12) = 1.5708
    c: Tangent(g5,g12) = 1.5708
    c: Coincident(g13,g8)
    c: Equal(g13,g12)
    c: Equal(g14,g13)
    c: Coincident(g7,g14)
    c: Tangent(g7,g13) = 1.5708
    c: Coincident(g16,g5)
    c: Coincident(g16,g6)
    c: Equal(g16,g12)
    c: Diameter(g10) = 4.5
    c: Distance(g22,g2) = 16
    c: Vertical(g18)
    c: Horizontal(g17)
    c: Coincident(g16,g10)
    c: Coincident(g8,g12)
    c: Equal(g15,g14)
    c: Diameter(g12) = 8
    c: Angle(g5,g8) = 2.61799
    c: PointOnObject(g20,g17)
    c: PointOnObject(g20,g18)
    c: Tangent(g17,g19) = 1.5708
    c: Tangent(g18,g19) = -1.5708
    c: PointOnObject(g22,g0)
    c: Tangent(g0,g21) = -1.5708
    c: Equal(g19,g21)
    c: Radius(g21) = 5
    c: PointOnObject(g24,g5)
    c: PointOnObject(g24,g18)
    c: Tangent(g5,g23) = 1.5708
    c: Tangent(g18,g23) = -1.5708
    c: Equal(g23,g15)
    c: Tangent(g15,g0) = -1.5708
    c: Tangent(g7,g15) = 1.5708
    c: Angle(g8,g7) = 2.61799
    c: Tangent(g21,g17) = 1.5708
    c: Equal(g5,g7)
    c: Horizontal(g1,g17)
    c: Distance(g18,g0) = 82
    c: Tangent(g6,g14) = 1.5708
FEATURE [PartDesign::Pad] Pad
  Direction = (0,0,1)
  Length = 8.7
  Length2 = 10
  Profile = -> Sketch
  ReferenceAxis = -> Sketch [N_Axis]
  Refine = true
  Suppressed = false
  Type = 0
  expr: Length = <<variables>>#Spreadsheet.claw_base_thickness
FEATURE [Sketcher::SketchObject] Sketch001
  ArcFitTolerance = 1e-06
  ExternalGeometry = -> [Pad]
  ExternalTypes = [0]
  FullyConstrained = true
  MakeInternals = false
  MapMode = 5
  Placement = pos=(0,0,8.7) rot=(0,0,1;0rad)
  expr: Constraints[20] = variables#Spreadsheet.servo_holes_to_spline
  expr: Constraints[8] = variables#Spreadsheet.servo_holes_horiz_dist
  expr: Constraints[9] = variables#Spreadsheet.servo_holes_vert_dist
  sketch-geometry (48):
    g0: LineSegment [constr] StartX=-17.25 StartY=-4.95 StartZ=0 EndX=32.25 EndY=-4.95 EndZ=0
    g1: LineSegment [constr] StartX=32.25 StartY=-4.95 StartZ=0 EndX=32.25 EndY=4.95 EndZ=0
    g2: LineSegment [constr] StartX=32.25 StartY=4.95 StartZ=0 EndX=-17.25 EndY=4.95 EndZ=0
    g3: LineSegment [constr] StartX=-17.25 StartY=4.95 StartZ=0 EndX=-17.25 EndY=-4.95 EndZ=0
    g4: Circle CenterX=32.25 CenterY=4.95 CenterZ=0 NormalX=0 NormalY=0 NormalZ=1 AngleXU=0 Radius=2.25
    g5: Circle CenterX=32.25 CenterY=-4.95 CenterZ=0 NormalX=0 NormalY=0 NormalZ=1 AngleXU=0 Radius=2.25
    g6: Circle CenterX=-17.25 CenterY=-4.95 CenterZ=0 NormalX=0 NormalY=0 NormalZ=1 AngleXU=0 Radius=2.25
    g7: Circle CenterX=-17.25 CenterY=4.95 CenterZ=0 NormalX=0 NormalY=0 NormalZ=1 AngleXU=0 Radius=2.25
    g8: GeomPoint X=32.25 Y=0 Z=0
    g9: GeomPoint X=17.5 Y=7.65474e-11 Z=0
    g10: LineSegment StartX=-14.25 StartY=15.5 StartZ=0 EndX=-24.25 EndY=15.5 EndZ=0
    g11: LineSegment StartX=-25.25 StartY=14.5 StartZ=0 EndX=-25.25 EndY=-14.5 EndZ=0
    g12: LineSegment StartX=-24.25 StartY=-15.5 StartZ=0 EndX=-14.25 EndY=-15.5 EndZ=0
    g13: LineSegment StartX=-13.25 StartY=-14.5 StartZ=0 EndX=-13.25 EndY=14.5 EndZ=0
    g14: LineSegment [constr] StartX=-17.25 StartY=0 StartZ=0 EndX=-13.25 EndY=0 EndZ=0
    g15: LineSegment StartX=29.25 StartY=-15.5 StartZ=0 EndX=39.25 EndY=-15.5 EndZ=0
    g16: LineSegment StartX=40.25 StartY=-14.5 StartZ=0 EndX=40.25 EndY=14.5 EndZ=0
    g17: LineSegment StartX=39.25 StartY=15.5 StartZ=0 EndX=29.25 EndY=15.5 EndZ=0
    g18: GeomPoint X=28.25 Y=0 Z=0
    g19: LineSegment [constr] StartX=28.25 StartY=0 StartZ=0 EndX=32.25 EndY=0 EndZ=0
    g20: LineSegment StartX=28.25 StartY=14.5 StartZ=0 EndX=28.25 EndY=-14.5 EndZ=0
    g21: GeomPoint X=7.5 Y=0 Z=0
    g22: ArcOfCircle CenterX=-24.25 CenterY=14.5 CenterZ=0 NormalX=0 NormalY=0 NormalZ=1 AngleXU=0 Radius=1 StartAngle=1.5708 EndAngle=3.14159
    g23: GeomPoint [constr] X=-25.25 Y=15.5 Z=0
    g24: ArcOfCircle CenterX=-14.25 CenterY=14.5 CenterZ=0 NormalX=0 NormalY=0 NormalZ=1 AngleXU=0 Radius=1 StartAngle=8e-16 EndAngle=1.5708
    g25: GeomPoint [constr] X=-13.25 Y=15.5 Z=0
    g26: ArcOfCircle CenterX=-14.25 CenterY=-14.5 CenterZ=0 NormalX=0 NormalY=0 NormalZ=1 AngleXU=0 Radius=1 StartAngle=4.71239 EndAngle=6.28319
    g27: GeomPoint [constr] X=-13.25 Y=-15.5 Z=0
    g28: ArcOfCircle CenterX=-24.25 CenterY=-14.5 CenterZ=0 NormalX=0 NormalY=0 NormalZ=1 AngleXU=0 Radius=1 StartAngle=3.14159 EndAngle=4.71239
    g29: GeomPoint [constr] X=-25.25 Y=-15.5 Z=0
    g30: ArcOfCircle CenterX=29.25 CenterY=14.5 CenterZ=0 NormalX=0 NormalY=0 NormalZ=1 AngleXU=0 Radius=1 StartAngle=1.5708 EndAngle=3.14159
    g31: GeomPoint [constr] X=28.25 Y=15.5 Z=0
    g32: ArcOfCircle CenterX=39.25 CenterY=14.5 CenterZ=0 NormalX=0 NormalY=0 NormalZ=1 AngleXU=0 Radius=1 StartAngle=-9e-16 EndAngle=1.5708
    g33: GeomPoint [constr] X=40.25 Y=15.5 Z=0
    g34: ArcOfCircle CenterX=39.25 CenterY=-14.5 CenterZ=0 NormalX=0 NormalY=0 NormalZ=1 AngleXU=0 Radius=1 StartAngle=4.71239 EndAngle=6.28319
    g35: GeomPoint [constr] X=40.25 Y=-15.5 Z=0
    g36: ArcOfCircle CenterX=29.25 CenterY=-14.5 CenterZ=0 NormalX=0 NormalY=0 NormalZ=1 AngleXU=0 Radius=1 StartAngle=3.14159 EndAngle=4.71239
    g37: GeomPoint [constr] X=28.25 Y=-15.5 Z=0
    g38: GeomPoint X=-25.25 Y=-1.3e-15 Z=0
    g39: GeomPoint X=-19.25 Y=-7e-16 Z=0
    g40: Circle CenterX=-19.25 CenterY=-12.5 CenterZ=0 NormalX=0 NormalY=0 NormalZ=1 AngleXU=0 Radius=2.25
    g41: Circle CenterX=-19.25 CenterY=12.5 CenterZ=0 NormalX=0 NormalY=0 NormalZ=1 AngleXU=0 Radius=2.25
    g42: LineSegment [constr] StartX=-19.25 StartY=-12.5 StartZ=0 EndX=-19.25 EndY=-15.5 EndZ=0
    g43: LineSegment [constr] StartX=-19.25 StartY=12.5 StartZ=0 EndX=-19.25 EndY=15.5 EndZ=0
    g44: LineSegment [constr] StartX=34.25 StartY=-15.5 StartZ=0 EndX=34.25 EndY=-12.5 EndZ=0
    g45: LineSegment [constr] StartX=34.25 StartY=15.5 StartZ=0 EndX=34.25 EndY=12.5 EndZ=0
    g46: Circle CenterX=34.25 CenterY=-12.5 CenterZ=0 NormalX=0 NormalY=0 NormalZ=1 AngleXU=0 Radius=2.25
    g47: Circle CenterX=34.25 CenterY=12.5 CenterZ=0 NormalX=0 NormalY=0 NormalZ=1 AngleXU=0 Radius=2.25
  constraints (109):
    c: Coincident(g0,g1)
    c: Coincident(g1,g2)
    c: Coincident(g2,g3)
    c: Coincident(g3,g0)
    c: Horizontal(g0)
    c: Horizontal(g2)
    c: Vertical(g1)
    c: Vertical(g3)
    c: DistanceX(g2,g2) = 49.5
    c: DistanceY(g1,g1) = 9.9
    c: Coincident(g4,g1)
    c: Coincident(g5,g0)
    c: Coincident(g6,g0)
    c: Diameter(g7) = 4.5
    c: Coincident(g7,g2)
    c: Equal(g7,g6)
    c: Equal(g6,g5)
    c: Equal(g5,g4)
    c: Symmetric(g1,g1,g8)
    c: PointOnObject(g8,g-1)
    c: DistanceX(g9,g8) = 14.75
    c: Horizontal(g10)
    c: Horizontal(g12)
    c: Vertical(g11)
    c: Vertical(g13)
    c: Distance(g23,g25) = 12
    c: Distance(g25,g27) = 31
    c: Symmetric(g27,g25,g14)
    c: Horizontal(g14)
    c: Vertical(g16)
    c: Horizontal(g15)
    c: Horizontal(g17)
    c: Coincident(g19,g8)
    c: Coincident(g18,g19)
    c: Horizontal(g19)
    c: Equal(g19,g14)
    c: Vertical(g20)
    c: Symmetric(g3,g3,g14)
    c: DistanceX(g14,g14) = 4
    c: Symmetric(g31,g37,g18)
    c: Symmetric(g14,g18,g21)
    c: PointOnObject(g23,g10)
    c: PointOnObject(g23,g11)
    c: Tangent(g10,g22) = -1.5708
    c: Tangent(g11,g22) = -1.5708
    c: PointOnObject(g25,g10)
    c: PointOnObject(g25,g13)
    c: Tangent(g10,g24) = -1.5708
    c: Tangent(g13,g24) = -1.5708
    c: PointOnObject(g27,g12)
    c: PointOnObject(g27,g13)
    c: Tangent(g12,g26) = -1.5708
    c: Tangent(g13,g26) = -1.5708
    c: PointOnObject(g29,g11)
    c: PointOnObject(g29,g12)
    c: Tangent(g11,g28) = -1.5708
    c: Tangent(g12,g28) = -1.5708
    c: Equal(g22,g24)
    c: Equal(g24,g26)
    c: Equal(g26,g28)
    c: Radius(g28) = 1
    c: Horizontal(g27,g37)
    c: PointOnObject(g31,g17)
    c: PointOnObject(g31,g20)
    c: Tangent(g17,g30) = -1.5708
    c: Tangent(g20,g30) = -1.5708
    c: PointOnObject(g33,g16)
    c: PointOnObject(g33,g17)
    c: Tangent(g16,g32) = -1.5708
    c: Tangent(g17,g32) = -1.5708
    c: PointOnObject(g35,g15)
    c: PointOnObject(g35,g16)
    c: Tangent(g15,g34) = -1.5708
    c: Tangent(g16,g34) = -1.5708
    c: PointOnObject(g37,g15)
    c: PointOnObject(g37,g20)
    c: Tangent(g15,g36) = -1.5708
    c: Tangent(g20,g36) = -1.5708
    c: Equal(g36,g34)
    c: Equal(g34,g32)
    c: Equal(g32,g30)
    c: Equal(g30,g24)
    c: Equal(g15,g12)
    c: Symmetric(g11,g11,g38)
    c: Symmetric(g38,g14,g39)
    c: Vertical(g41,g39)
    c: Vertical(g39,g40)
    c: Equal(g40,g6)
    c: Equal(g41,g7)
    c: Coincident(g42,g40)
    c: Symmetric(g12,g12,g42)
    c: DistanceY(g42,g42) = 3
    c: Coincident(g43,g41)
    c: Symmetric(g10,g10,g43)
    c: Equal(g43,g42)
    c: Symmetric(g15,g15,g44)
    c: Symmetric(g17,g17,g45)
    c: Vertical(g45)
    c: Vertical(g44)
    c: Equal(g44,g45)
    c: Equal(g42,g44)
    c: Coincident(g46,g44)
    c: Coincident(g47,g45)
    c: Equal(g47,g4)
    c: Equal(g4,g46)
    c: DistanceY(g44,g-1) = 12.5  'structure_holes_y'
    c: DistanceX(g40,g44) = 53.5  'structure_holes_c2c'
    c: DistanceX(g41,g-1) = 19.25  'structure_hole_x'
    c: Coincident(g9,g-3)
FEATURE [PartDesign::Pad] Pad001
  BaseFeature = -> Pad
  Direction = (0,0,1)
  Length = 10
  Length2 = 10
  Profile = -> Sketch001
  ReferenceAxis = -> Sketch001 [N_Axis]
  Refine = true
  Suppressed = false
  Type = 0
FEATURE [PartDesign::CoordinateSystem] Local_CS
  AttacherType = Attacher::AttachEngine3D
  MapMode = 11
  Placement = pos=(-25,25,0) rot=(0,0,1;1.5708rad)
FEATURE [Sketcher::SketchObject] Sketch002
  ArcFitTolerance = 1e-06
  AttachmentSupport = -> [Pad001]
  ExternalGeometry = -> [Pad001]
  ExternalTypes = [0]
  FullyConstrained = true
  MakeInternals = false
  MapMode = 5
  Placement = pos=(0,0,18.7) rot=(0,0,1;0rad)
  sketch-geometry (6):
    g0: GeomPoint X=28.25 Y=-7e-16 Z=0
    g1: LineSegment [constr] StartX=28.25 StartY=-7e-16 StartZ=0 EndX=35.25 EndY=0 EndZ=0
    g2: LineSegment StartX=28.25 StartY=1.5 StartZ=0 EndX=35.25 EndY=1.5 EndZ=0
    g3: LineSegment StartX=35.25 StartY=1.5 StartZ=0 EndX=35.25 EndY=-1.5 EndZ=0
    g4: LineSegment StartX=35.25 StartY=-1.5 StartZ=0 EndX=28.25 EndY=-1.5 EndZ=0
    g5: LineSegment StartX=28.25 StartY=-1.5 StartZ=0 EndX=28.25 EndY=1.5 EndZ=0
  constraints (14):
    c: Distance(g1) = 7
    c: Coincident(g1,g0)
    c: PointOnObject(g1,g-1)
    c: Horizontal(g2)
    c: Coincident(g2,g3)
    c: Vertical(g3)
    c: Coincident(g3,g4)
    c: Symmetric(g3,g3,g1)
    c: DistanceY(g3,g3) = 3
    c: Coincident(g5,g4)
    c: Coincident(g5,g2)
    c: Symmetric(g5,g5,g0)
    c: Symmetric(g-3,g-3,g0)
    c: Vertical(g5)
FEATURE [Part::Feature] path8
  shape: bbox 9.031 x 11.29 x 4e-07 mm, 1 faces, 0 solids (baked)
FEATURE [Part::Feature] path7
  shape: bbox 4.516 x 4.516 x 4e-07 mm, 1 faces, 0 solids (baked)
FEATURE [Part::Feature] path009
  shape: bbox 4.516 x 4.516 x 4e-07 mm, 1 faces, 0 solids (baked)
FEATURE [Part::Feature] path3
  shape: bbox 9.031 x 11.29 x 4e-07 mm, 1 faces, 0 solids (baked)
FEATURE [Part::Feature] path9
  shape: bbox 6.773 x 9.031 x 4e-07 mm, 1 faces, 0 solids (baked)
FEATURE [Part::Compound] Compound
  Links = -> [path8,path7,path009,path3,path9]
FEATURE [Part::Scale] Scale
  Base = -> Compound
  Uniform = true
  UniformScale = 1.25
  XScale = 1
  YScale = 1
  ZScale = 1
FEATURE [PartDesign::Pocket] Pocket010
  BaseFeature = -> Pad001
  Direction = (0,0,-1)
  Length = 0
  Length2 = 5
  Profile = -> Sketch001 [Edge2,Edge1]
  ReferenceAxis = -> Sketch001 [N_Axis]
  Refine = true
  Suppressed = false
  Type = 3
  UpToFace = -> Pad001 [Face4]
FEATURE [PartDesign::Pocket] Pocket009
  BaseFeature = -> Pocket010
  Direction = (0,0,-1)
  Length = 0
  Length2 = 5
  Profile = -> Sketch001 [Edge21,Edge23,Edge24,Edge22]
  ReferenceAxis = -> Sketch001 [N_Axis]
  Refine = true
  Suppressed = false
  Type = 3
  UpToFace = -> Pocket010 [Face4]
FEATURE [PartDesign::Hole] Hole
  BaseFeature = -> Pocket009
  CustomThreadClearance = 0
  Depth = 25
  DepthType = 0
  Diameter = 4.5
  DrillForDepth = false
  DrillPoint = 1
  DrillPointAngle = 118
  HoleCutCountersinkAngle = 90
  HoleCutCustomValues = false
  HoleCutDepth = 0.5
  HoleCutDiameter = 10
  HoleCutType = 2
  ModelThread = false
  Profile = -> Pocket009 [Edge28,Edge22,Edge24,Edge30]
  Refine = true
  Reversed = true
  Suppressed = false
  Tapered = false
  TaperedAngle = 90
  ThreadClass = 0
  ThreadDepth = 25
  ThreadDepthType = 0
  ThreadDirection = 0
  ThreadFit = 0
  ThreadSize = 11
  ThreadType = 1
  Threaded = false
  UseCustomThreadClearance = false
FEATURE [PartDesign::Pocket] Pocket
  BaseFeature = -> Hole
  Direction = (0,0,-1)
  Length = 2.25
  Length2 = 5
  Profile = -> Sketch002
  ReferenceAxis = -> Sketch002 [N_Axis]
  Refine = true
  Suppressed = false
  Type = 0
FEATURE [PartDesign::Plane] DatumPlane
  AttachmentSupport = -> [Sketch001,Pocket]
  Length = 64.3923
  MapMode = 6
  Placement = pos=(7.5,0,8.7) rot=(0.57735,0.57735,0.57735;2.0944rad)
  ResizeMode = 0
  Width = 60.3923
FEATURE [PartDesign::Mirrored] Mirrored
  BaseFeature = -> Pocket
  MirrorPlane = -> DatumPlane
  Originals = -> [Pocket]
  Refine = true
  Suppressed = false
  TransformMode = 0
FEATURE [Sketcher::SketchObject] Sketch003
  ArcFitTolerance = 1e-06
  AttachmentOffset = pos=(0,0,-3) rot=(0,0,1;0rad)
  AttachmentSupport = -> [Mirrored]
  ExternalGeometry = -> [Mirrored,Sketch001]
  ExternalTypes = [0]
  FullyConstrained = true
  MakeInternals = false
  MapMode = 5
  Placement = pos=(0,0,15.7) rot=(0,0,1;0rad)
  sketch-geometry (22):
    g0: LineSegment StartX=-15.2004 StartY=-8.5 StartZ=0 EndX=-13.1508 EndY=-4.95 EndZ=0
    g1: LineSegment StartX=-13.1508 StartY=-4.95 StartZ=0 EndX=-15.2004 EndY=-1.4 EndZ=0
    g2: LineSegment StartX=-15.2004 StartY=-1.4 StartZ=0 EndX=-19.2996 EndY=-1.4 EndZ=0
    g3: LineSegment [constr] StartX=-19.2996 StartY=-1.4 StartZ=0 EndX=-21.3492 EndY=-4.95 EndZ=0
    g4: LineSegment [constr] StartX=-21.3492 StartY=-4.95 StartZ=0 EndX=-19.2996 EndY=-8.5 EndZ=0
    g5: LineSegment StartX=-19.2996 StartY=-8.5 StartZ=0 EndX=-15.2004 EndY=-8.5 EndZ=0
    g6: Circle [constr] CenterX=-17.25 CenterY=-4.95 CenterZ=0 NormalX=0 NormalY=0 NormalZ=1 AngleXU=0 Radius=4.09919
    g7: Circle [constr] CenterX=-17.25 CenterY=-4.95 CenterZ=0 NormalX=0 NormalY=0 NormalZ=1 AngleXU=0 Radius=3.55
    g8: LineSegment StartX=-15.2004 StartY=1.4 StartZ=0 EndX=-13.1508 EndY=4.95 EndZ=0
    g9: LineSegment StartX=-13.1508 StartY=4.95 StartZ=0 EndX=-15.2004 EndY=8.5 EndZ=0
    g10: LineSegment StartX=-15.2004 StartY=8.5 StartZ=0 EndX=-19.2996 EndY=8.5 EndZ=0
    g11: LineSegment [constr] StartX=-19.2996 StartY=8.5 StartZ=0 EndX=-21.3492 EndY=4.95 EndZ=0
    g12: LineSegment [constr] StartX=-21.3492 StartY=4.95 StartZ=0 EndX=-19.2996 EndY=1.4 EndZ=0
    g13: LineSegment StartX=-19.2996 StartY=1.4 StartZ=0 EndX=-15.2004 EndY=1.4 EndZ=0
    g14: Circle [constr] CenterX=-17.25 CenterY=4.95 CenterZ=0 NormalX=0 NormalY=0 NormalZ=1 AngleXU=0 Radius=4.09919
    g15: Circle [constr] CenterX=-17.25 CenterY=4.95 CenterZ=0 NormalX=0 NormalY=0 NormalZ=1 AngleXU=0 Radius=3.55
    g16: LineSegment StartX=-19.2996 StartY=-1.4 StartZ=0 EndX=-25.25 EndY=-1.4 EndZ=0
    g17: LineSegment StartX=-19.2996 StartY=-8.5 StartZ=0 EndX=-25.25 EndY=-8.5 EndZ=0
    g18: LineSegment StartX=-19.2996 StartY=1.4 StartZ=0 EndX=-25.25 EndY=1.4 EndZ=0
    g19: LineSegment StartX=-19.2996 StartY=8.5 StartZ=0 EndX=-25.25 EndY=8.5 EndZ=0
    g20: LineSegment StartX=-25.25 StartY=8.5 StartZ=0 EndX=-25.25 EndY=1.4 EndZ=0
    g21: LineSegment StartX=-25.25 StartY=-1.4 StartZ=0 EndX=-25.25 EndY=-8.5 EndZ=0
  constraints (52):
    c: Coincident(g0,g1)
    c: Coincident(g1,g2)
    c: Coincident(g2,g3)
    c: Coincident(g3,g4)
    c: Coincident(g4,g5)
    c: Coincident(g5,g0)
    c: Equal(g0, g1-g5) x5
    c: PointOnObject(g0,g6)
    c: PointOnObject(g1,g6)
    c: PointOnObject(g2,g6)
    c: PointOnObject(g3,g6)
    c: PointOnObject(g4,g6)
    c: PointOnObject(g5,g6)
    c: Coincident(g6,g-4)
    c: Horizontal(g5)
    c: Coincident(g7,g6)
    c: Tangent(g7,g1)
    c: Diameter(g7) = 7.1
    c: Coincident(g8,g9)
    c: Coincident(g9,g10)
    c: Coincident(g10,g11)
    c: Coincident(g11,g12)
    c: Coincident(g12,g13)
    c: Coincident(g13,g8)
    c: Equal(g8, g9-g13) x5
    c: PointOnObject(g8,g14)
    c: PointOnObject(g9,g14)
    c: PointOnObject(g10,g14)
    c: PointOnObject(g11,g14)
    c: PointOnObject(g12,g14)
    c: PointOnObject(g13,g14)
    c: Coincident(g14,g-3)
    c: Horizontal(g13)
    c: Coincident(g15,g14)
    c: Tangent(g15,g10)
    c: Equal(g15,g7)
    c: Coincident(g16,g2)
    c: Horizontal(g16)
    c: Coincident(g17,g4)
    c: Horizontal(g17)
    c: Coincident(g18,g12)
    c: Horizontal(g18)
    c: Coincident(g19,g10)
    c: Horizontal(g19)
    c: Coincident(g20,g19)
    c: Coincident(g20,g18)
    c: Coincident(g21,g16)
    c: Coincident(g21,g17)
    c: Vertical(g20)
    c: Vertical(g18,g16)
    c: Vertical(g21)
    c: PointOnObject(g16,g-5)
FEATURE [PartDesign::Pocket] Pocket001
  BaseFeature = -> Mirrored
  Direction = (0,0,-1)
  Length = 6
  Length2 = 5
  Profile = -> Sketch003
  ReferenceAxis = -> Sketch003 [N_Axis]
  Refine = true
  Suppressed = false
  Type = 0
FEATURE [PartDesign::Mirrored] Mirrored001
  BaseFeature = -> Pocket001
  MirrorPlane = -> DatumPlane
  Originals = -> [Pocket001]
  Refine = true
  Suppressed = false
  TransformMode = 0
FEATURE [PartDesign::Body] Body  label="Claw Base Body"
  AllowCompound = false
  Group = -> [Sketch,Pad,Sketch001,Pad001,Local_CS,Sketch002,Pocket010,Pocket009,Hole,Pocket,DatumPlane,Mirrored,Sketch003,Pocket001,Mirrored001]
  Origin = -> Origin
  Tip = -> Mirrored001
FEATURE [App::Point] Origin001  label="Origin"
  Role = Origin
---- part claw-pinchers.FCStd = doc fcstd_a9d89a299ddd ----
FCSTD DOCUMENT  (FreeCAD 1.1R39747 (Git))
Label: claw-pinchers
License: All rights reserved
LicenseURL: https://en.wikipedia.org/wiki/All_rights_reserved
objects: Sketcher::SketchObject×16, PartDesign::Pocket×11, PartDesign::Pad×8, PartDesign::Fillet×4, PartDesign::FeaturePython×2, Part::Part2DObjectPython×2, PartDesign::Hole×2, PartDesign::Body×2, App::Point×2, PartDesign::SubShapeBinder×1
note: 116 computed .brp shape members not serialized (recipe doc carries the construction recipe); baked Part::Feature solids carry a one-line shape summary decoded from their .brp
EXTERNAL_REF file=variables.FCStd obj=Spreadsheet

FEATURE [PartDesign::FeaturePython] InvoluteGear  # WARN: FeaturePython — macro-defined, semantics opaque (R4)
  AttacherType = Attacher::AttachEngine3D
  Suppressed = false
  angular_backlash = 0
  backlash = 0
  beta = 0
  clearance = 0.25
  da = 37
  df = 32.5
  double_helix = false
  dw = 35
  head = 0
  head_fillet = 0
  height = 8.4
  module = 1
  num_teeth = 35
  numpoints = 20
  pressure_angle = 20
  properties_from_tool = false
  reversed_backlash = false
  root_fillet = 0
  shift = 0
  simple = false
  transverse_pitch = 3.14159
  traverse_module = 1
  undercut = false
  version = 1.3.0
  expr: angular_backlash = backlash / dw * 360 ° / pi
  expr: num_teeth = variables#Spreadsheet.claw_pincher_c2c
FEATURE [Sketcher::SketchObject] Sketch
  ArcFitTolerance = 1e-06
  AttachmentSupport = -> [InvoluteGear]
  ExternalTypes = [0]
  FullyConstrained = true
  MakeInternals = false
  MapMode = 5
  Placement = pos=(0,0,8.4) rot=(0,0,1;0rad)
  expr: Constraints[17] = variables#Spreadsheet.claw_pincher_length
  expr: Constraints[1] = variables#Spreadsheet.claw_pincher_c2c + 2
  sketch-geometry (16):
    g0: ArcOfCircle CenterX=0 CenterY=0 CenterZ=0 NormalX=0 NormalY=0 NormalZ=1 AngleXU=0 Radius=18.5 StartAngle=1.5708 EndAngle=2.04818
    g1: LineSegment StartX=0 StartY=0 StartZ=0 EndX=-18.5 EndY=0 EndZ=0
    g2: LineSegment StartX=0 StartY=0 StartZ=0 EndX=0 EndY=18.5 EndZ=0
    g3: LineSegment StartX=-18.5 StartY=0 StartZ=0 EndX=-18.5 EndY=31.8416 EndZ=0
    g4: ArcOfCircle CenterX=0 CenterY=0 CenterZ=0 NormalX=0 NormalY=0 NormalZ=1 AngleXU=0 Radius=51.8191 StartAngle=1.52253 EndAngle=1.95478
    g5: LineSegment StartX=2.5 StartY=51.7588 StartZ=0 EndX=2.5 EndY=48.7588 EndZ=0
    g6: LineSegment StartX=2.5 StartY=48.7588 StartZ=0 EndX=-8.5 EndY=37.7588 EndZ=0
    g7: LineSegment StartX=-8.5 StartY=37.7588 StartZ=0 EndX=-8.5 EndY=16.4317 EndZ=0
    g8: LineSegment [constr] StartX=-13.5 StartY=12.6491 StartZ=0 EndX=-13.5 EndY=47.6491 EndZ=0
    g9: LineSegment [constr] StartX=-18.5 StartY=47.6491 StartZ=0 EndX=-8.5 EndY=47.6491 EndZ=0
    g10: LineSegment StartX=-19.4124 StartY=48.0456 StartZ=0 EndX=-21.2839 EndY=34.7295 EndZ=0
    g11: LineSegment StartX=-19.947 StartY=33.1916 StartZ=0 EndX=-19.85 EndY=33.1916 EndZ=0
    g12: ArcOfCircle CenterX=-19.85 CenterY=31.8416 CenterZ=0 NormalX=0 NormalY=0 NormalZ=1 AngleXU=0 Radius=1.35 StartAngle=-9e-16 EndAngle=1.5708
    g13: GeomPoint [constr] X=-18.5 Y=33.1916 Z=0
    g14: ArcOfCircle CenterX=-19.947 CenterY=34.5416 CenterZ=0 NormalX=0 NormalY=0 NormalZ=1 AngleXU=0 Radius=1.35 StartAngle=3.00197 EndAngle=4.71239
    g15: GeomPoint [constr] X=-21.5 Y=33.1916 Z=0
  constraints (44):
    c: Coincident(g0,g-1)
    c: Diameter(g0) = 37
    c: Coincident(g1,g0)
    c: Horizontal(g1)
    c: Coincident(g2,g0)
    c: Vertical(g2)
    c: Coincident(g0,g2)
    c: Coincident(g3,g1)
    c: Vertical(g3)
    c: Coincident(g4,g0)
    c: Distance(g5) = 3
    c: Coincident(g5,g4)
    c: Vertical(g5)
    c: Coincident(g6,g5)
    c: Coincident(g7,g6)
    c: Vertical(g7)
    c: Vertical(g8)
    c: DistanceY(g8,g8) = 35
    c: Horizontal(g9)
    c: DistanceX(g9,g9) = 10
    c: Symmetric(g9,g9,g8)
    c: Vertical(g6,g9)
    c: DistanceX(g8,g4) = 16
    c: Angle(g9,g6) = 0.785398
    c: Coincident(g0,g7)
    c: PointOnObject(g1,g0)
    c: Horizontal(g11)
    c: PointOnObject(g9,g3)
    c: Coincident(g10,g4)
    c: Distance(g4,g9) = -4.17
    c: DistanceX(g15,g13) = 3
    c: Distance(g10,g15) = 15
    c: PointOnObject(g13,g3)
    c: PointOnObject(g13,g11)
    c: Tangent(g3,g12) = -1.5708
    c: Tangent(g11,g12) = 1.5708
    c: PointOnObject(g15,g10)
    c: PointOnObject(g15,g11)
    c: Tangent(g10,g14) = -1.5708
    c: Tangent(g11,g14) = -1.5708
    c: Angle(g10,g3) = 0.139626
    c: Equal(g12,g14)
    c: Radius(g12) = 1.35
    c: PointOnObject(g8,g0)
FEATURE [PartDesign::Pad] Pad
  BaseFeature = -> InvoluteGear
  Direction = (0,0,1)
  Length = 10
  Length2 = 10
  Profile = -> Sketch
  ReferenceAxis = -> Sketch [N_Axis]
  Refine = true
  Suppressed = false
  Type = 3
  UpToFace = -> InvoluteGear [Face211]
FEATURE [Sketcher::SketchObject] Sketch001
  ArcFitTolerance = 1e-06
  AttachmentSupport = -> [Pad]
  ExternalGeometry = -> [Sketch,Pad]
  ExternalTypes = [0]
  FullyConstrained = true
  MakeInternals = false
  MapMode = 5
  Placement = pos=(-18.5,0,0) rot=(0.57735,-0.57735,-0.57735;2.0944rad)
  sketch-geometry (6):
    g0: LineSegment [constr] StartX=-51.8191 StartY=0 StartZ=0 EndX=-51.8191 EndY=8.4 EndZ=0
    g1: LineSegment StartX=-51.8191 StartY=4.2 StartZ=0 EndX=-47.6191 EndY=8.4 EndZ=0
    g2: LineSegment StartX=-51.8191 StartY=4.2 StartZ=0 EndX=-47.6191 EndY=0 EndZ=0
    g3: LineSegment StartX=-47.6191 StartY=8.4 StartZ=0 EndX=-51.8191 EndY=8.4 EndZ=0
    g4: LineSegment StartX=-51.8191 StartY=8.4 StartZ=0 EndX=-51.8191 EndY=0 EndZ=0
    g5: LineSegment StartX=-51.8191 StartY=0 StartZ=0 EndX=-47.6191 EndY=0 EndZ=0
  constraints (14):
    c: Coincident(g0,g-4)
    c: Coincident(g0,g-3)
    c: Symmetric(g0,g0,g1)
    c: PointOnObject(g1,g-3)
    c: Coincident(g2,g1)
    c: PointOnObject(g2,g-4)
    c: Equal(g2,g1)
    c: Angle(g1,g0) = 0.785398
    c: Coincident(g1,g3)
    c: Coincident(g3,g0)
    c: Coincident(g3,g4)
    c: Coincident(g4,g0)
    c: Coincident(g4,g5)
    c: Coincident(g5,g2)
FEATURE [PartDesign::Pocket] Pocket
  BaseFeature = -> Pad
  Direction = (1,0,0)
  Length = 50
  Length2 = 5
  Midplane = true
  Profile = -> Sketch001
  ReferenceAxis = -> Sketch001 [N_Axis]
  Refine = true
  Suppressed = false
  Type = 0
FEATURE [PartDesign::FeaturePython] InvoluteGear001  # WARN: FeaturePython — macro-defined, semantics opaque (R4)
  AttacherType = Attacher::AttachEngine3D
  Placement = pos=(35,0,0) rot=(0,0,1;0rad)
  Suppressed = false
  angular_backlash = 0
  backlash = 0
  beta = 0
  clearance = 0.25
  da = 37
  df = 32.5
  double_helix = false
  dw = 35
  head = 0
  head_fillet = 0
  height = 8.4
  module = 1
  num_teeth = 35
  numpoints = 20
  pressure_angle = 20
  properties_from_tool = false
  reversed_backlash = false
  root_fillet = 0
  shift = 0
  simple = false
  transverse_pitch = 3.14159
  traverse_module = 1
  undercut = false
  version = 1.3.0
  expr: .Placement.Base.x = variables#Spreadsheet.claw_pincher_c2c
  expr: angular_backlash = backlash / dw * 360 ° / pi
  expr: height = InvoluteGear.height
  expr: num_teeth = variables#Spreadsheet.claw_pincher_c2c
FEATURE [Sketcher::SketchObject] Sketch002
  ArcFitTolerance = 1e-06
  AttachmentSupport = -> [Pocket]
  ExternalTypes = [0]
  FullyConstrained = true
  MakeInternals = false
  MapMode = 5
  Placement = pos=(0,0,8.4) rot=(0,0,1;0rad)
  sketch-geometry (9):
    g0: LineSegment [constr] StartX=-8 StartY=8 StartZ=0 EndX=-8 EndY=-8 EndZ=0
    g1: LineSegment [constr] StartX=-8 StartY=-8 StartZ=0 EndX=8 EndY=-8 EndZ=0
    g2: LineSegment [constr] StartX=8 StartY=-8 StartZ=0 EndX=8 EndY=8 EndZ=0
    g3: LineSegment [constr] StartX=8 StartY=8 StartZ=0 EndX=-8 EndY=8 EndZ=0
    g4: GeomPoint [constr] X=0 Y=0 Z=0
    g5: Circle CenterX=-8 CenterY=-8 CenterZ=0 NormalX=0 NormalY=0 NormalZ=1 AngleXU=0 Radius=2.25
    g6: Circle CenterX=8 CenterY=-8 CenterZ=0 NormalX=0 NormalY=0 NormalZ=1 AngleXU=0 Radius=2.25
    g7: Circle CenterX=8 CenterY=8 CenterZ=0 NormalX=0 NormalY=0 NormalZ=1 AngleXU=0 Radius=2.25
    g8: Circle CenterX=-8 CenterY=8 CenterZ=0 NormalX=0 NormalY=0 NormalZ=1 AngleXU=0 Radius=2.25
  constraints (20):
    c: Coincident(g0,g1)
    c: Coincident(g1,g2)
    c: Coincident(g2,g3)
    c: Coincident(g3,g0)
    c: Vertical(g0)
    c: Vertical(g2)
    c: Horizontal(g1)
    c: Horizontal(g3)
    c: Symmetric(g2,g0,g4)
    c: Distance(g0,g2) = 16
    c: Coincident(g4,g-1)
    c: Equal(g2,g1)
    c: Diameter(g5) = 4.5
    c: Coincident(g5,g0)
    c: Coincident(g6,g1)
    c: Coincident(g7,g2)
    c: Coincident(g8,g0)
    c: Equal(g8,g7)
    c: Equal(g7,g6)
    c: Equal(g6,g5)
FEATURE [PartDesign::Pocket] Pocket001
  BaseFeature = -> Pocket
  Direction = (0,0,-1)
  Length = 0
  Length2 = 5
  Profile = -> Sketch002
  ReferenceAxis = -> Sketch002 [N_Axis]
  Refine = true
  Suppressed = false
  Type = 3
  UpToFace = -> Pocket [Face4]
FEATURE [Sketcher::SketchObject] Sketch003
  ArcFitTolerance = 1e-06
  AttachmentSupport = -> [Pocket001]
  ExternalTypes = [0]
  FullyConstrained = true
  MakeInternals = false
  MapMode = 5
  Placement = pos=(0,0,0) rot=(1,0,0;3.14159rad)
  sketch-geometry (1):
    g0: Circle CenterX=0 CenterY=0 CenterZ=0 NormalX=0 NormalY=0 NormalZ=1 AngleXU=0 Radius=4.75
  constraints (2):
    c: Diameter(g0) = 9.5
    c: Coincident(g0,g-1)
FEATURE [PartDesign::Pad] Pad001
  BaseFeature = -> Pocket001
  Direction = (0,0,-1)
  Length = 4.3
  Length2 = 10
  Profile = -> Sketch003
  ReferenceAxis = -> Sketch003 [N_Axis]
  Refine = true
  Suppressed = false
  Type = 0
  expr: Length = 4.6 - variables#Spreadsheet.tollerance
FEATURE [PartDesign::Fillet] Fillet
  Base = -> Pad001 [Edge186,Edge542]
  BaseFeature = -> Pad001
  Radius = 0.75
  Refine = true
  SupportTransform = false
  Suppressed = false
  UseAllEdges = false
FEATURE [Sketcher::SketchObject] Sketch004
  ArcFitTolerance = 1e-06
  AttachmentSupport = -> [Fillet]
  ExternalTypes = [0]
  FullyConstrained = true
  MakeInternals = false
  MapMode = 5
  Placement = pos=(0,0,-4.3) rot=(1,0,0;3.14159rad)
  expr: Constraints[0] = variables#Spreadsheet.shaft_diam
  sketch-geometry (1):
    g0: Circle CenterX=0 CenterY=0 CenterZ=0 NormalX=0 NormalY=0 NormalZ=1 AngleXU=0 Radius=3.9
  constraints (2):
    c: Diameter(g0) = 7.8
    c: Coincident(g0,g-1)
FEATURE [PartDesign::Pad] Pad002
  BaseFeature = -> Fillet
  Direction = (0,0,-1)
  Length = 6
  Length2 = 10
  Profile = -> Sketch004
  ReferenceAxis = -> Sketch004 [N_Axis]
  Refine = true
  Suppressed = false
  Type = 0
FEATURE [Sketcher::SketchObject] Sketch005
  ArcFitTolerance = 1e-06
  AttachmentSupport = -> [Pad002]
  ExternalGeometry = -> [Pad002]
  ExternalTypes = [0]
  FullyConstrained = true
  MakeInternals = false
  MapMode = 5
  Placement = pos=(0,0,0) rot=(1,0,0;3.14159rad)
  sketch-geometry (4):
    g0: Circle CenterX=-8 CenterY=-8 CenterZ=0 NormalX=0 NormalY=0 NormalZ=1 AngleXU=0 Radius=4.5
    g1: Circle CenterX=8 CenterY=-8 CenterZ=0 NormalX=0 NormalY=0 NormalZ=1 AngleXU=0 Radius=4.5
    g2: Circle CenterX=8 CenterY=8 CenterZ=0 NormalX=0 NormalY=0 NormalZ=1 AngleXU=0 Radius=4.5
    g3: Circle CenterX=-8 CenterY=8 CenterZ=0 NormalX=0 NormalY=0 NormalZ=1 AngleXU=0 Radius=4.5
  constraints (8):
    c: Diameter(g0) = 9
    c: Coincident(g0,g-6)
    c: Coincident(g1,g-5)
    c: Coincident(g2,g-4)
    c: Coincident(g3,g-3)
    c: Equal(g3,g2)
    c: Equal(g2,g1)
    c: Equal(g1,g0)
FEATURE [PartDesign::Pocket] Pocket002
  BaseFeature = -> Pad002
  Direction = (0,0,1)
  Length = 1.5
  Length2 = 5
  Profile = -> Sketch005
  ReferenceAxis = -> Sketch005 [N_Axis]
  Refine = true
  Suppressed = false
  Type = 0
FEATURE [PartDesign::SubShapeBinder] Binder
  BindCopyOnChange = 0
  BindMode = 0
  ClaimChildren = false
  Context = -> Body001 [Binder.]
  Fuse = false
  MakeFace = true
  OffsetFill = false
  OffsetIntersection = false
  OffsetJoinType = 0
  OffsetOpenResult = false
  PartialLoad = false
  Refine = true
  Relative = true
  Support = -> [Body]
  _Version = 2
FEATURE [Sketcher::SketchObject] Sketch006
  ArcFitTolerance = 1e-06
  AttachmentSupport = -> [InvoluteGear001]
  ExternalGeometry = -> [Binder]
  ExternalTypes = [0]
  FullyConstrained = true
  MakeInternals = false
  MapMode = 5
  Placement = pos=(35,0,8.4) rot=(0,0,1;0rad)
  expr: Constraints[2] = (variables#Spreadsheet.claw_pincher_c2c + 2) / 2
  sketch-geometry (17):
    g0: LineSegment StartX=0 StartY=0 StartZ=0 EndX=18.5 EndY=0 EndZ=0
    g1: LineSegment StartX=0 StartY=18.5 StartZ=0 EndX=0 EndY=0 EndZ=0
    g2: LineSegment StartX=18.5 StartY=0 StartZ=0 EndX=18.5 EndY=31.8416 EndZ=0
    g3: ArcOfCircle CenterX=19.85 CenterY=31.8416 CenterZ=0 NormalX=0 NormalY=0 NormalZ=1 AngleXU=0 Radius=1.35 StartAngle=1.5708 EndAngle=3.14159
    g4: LineSegment StartX=19.85 StartY=33.1916 StartZ=0 EndX=19.947 EndY=33.1916 EndZ=0
    g5: ArcOfCircle CenterX=19.947 CenterY=34.5416 CenterZ=0 NormalX=0 NormalY=0 NormalZ=1 AngleXU=0 Radius=1.35 StartAngle=4.71239 EndAngle=6.42281
    g6: LineSegment StartX=21.2839 StartY=34.7295 StartZ=0 EndX=19.4124 EndY=48.0456 EndZ=0
    g7: LineSegment [constr] StartX=-56.2839 StartY=34.7295 StartZ=0 EndX=-54.4124 EndY=48.0456 EndZ=0
    g8: LineSegment StartX=8.5 StartY=16.4317 StartZ=0 EndX=8.5 EndY=37.7588 EndZ=0
    g9: LineSegment StartX=8.5 StartY=37.7588 StartZ=0 EndX=-2.5 EndY=48.7588 EndZ=0
    g10: LineSegment [constr] StartX=8.5 StartY=27.0952 StartZ=0 EndX=18.5 EndY=27.0952 EndZ=0
    g11: LineSegment [constr] StartX=-53.5 StartY=15.9208 StartZ=0 EndX=-43.5 EndY=15.9208 EndZ=0
    g12: LineSegment [constr] StartX=-32.5 StartY=48.7588 StartZ=0 EndX=-43.5 EndY=37.7588 EndZ=0
    g13: LineSegment StartX=-2.5 StartY=48.7588 StartZ=0 EndX=-2.5 EndY=51.7588 EndZ=0
    g14: ArcOfCircle CenterX=0 CenterY=0 CenterZ=0 NormalX=0 NormalY=0 NormalZ=1 AngleXU=0 Radius=51.8191 StartAngle=1.18681 EndAngle=1.61906
    g15: ArcOfCircle CenterX=0 CenterY=0 CenterZ=0 NormalX=0 NormalY=0 NormalZ=1 AngleXU=0 Radius=18.5 StartAngle=1.09341 EndAngle=1.5708
    g16: LineSegment [constr] StartX=-54.4124 StartY=48.0456 StartZ=0 EndX=-32.5 EndY=51.7588 EndZ=0
  constraints (46):
    c: Coincident(g0,g-1)
    c: PointOnObject(g0,g-1)
    c: DistanceX(g0,g0) = 18.5
    c: PointOnObject(g1,g-2)
    c: Coincident(g2,g0)
    c: Vertical(g2)
    c: Equal(g5,g3)
    c: Equal(g3,g-5)
    c: Equal(g4,g-7)
    c: Horizontal(g4)
    c: Tangent(g3,g2) = 1.5708
    c: Tangent(g4,g3) = 1.5708
    c: Tangent(g5,g4) = -1.5708
    c: Coincident(g6,g5)
    c: Horizontal(g-10,g6)
    c: Coincident(g7,g-8)
    c: Coincident(g7,g-10)
    c: Vertical(g8)
    c: Equal(g8,g-4)
    c: Coincident(g9,g8)
    c: Symmetric(g8,g8,g10)
    c: PointOnObject(g10,g2)
    c: Horizontal(g10)
    c: Symmetric(g-3,g-3,g11)
    c: PointOnObject(g11,g-4)
    c: Horizontal(g11)
    c: Equal(g11,g10)
    c: Coincident(g12,g-14)
    c: Coincident(g12,g-15)
    c: Coincident(g13,g9)
    c: Vertical(g13)
    c: Horizontal(g13,g-13)
    c: Coincident(g14,g13)
    c: Coincident(g14,g6)
    c: Coincident(g14,g0)
    c: Horizontal(g5,g7)
    c: Horizontal(g2,g-5)
    c: Coincident(g15,g8)
    c: Coincident(g15,g1)
    c: Coincident(g1,g15)
    c: Coincident(g0,g1)
    c: Horizontal(g8,g-4)
    c: Coincident(g16,g7)
    c: Coincident(g16,g-13)
    c: Horizontal(g9,g12)
    c: Equal(g9,g12)
FEATURE [PartDesign::Pad] Pad003
  BaseFeature = -> InvoluteGear001
  Direction = (0,0,1)
  Length = 10
  Length2 = 10
  Placement = pos=(35,0,0) rot=(0,0,1;0rad)
  Profile = -> Sketch006
  ReferenceAxis = -> Sketch006 [N_Axis]
  Refine = true
  Suppressed = false
  Type = 3
  UpToFace = -> InvoluteGear001 [Face211]
FEATURE [Sketcher::SketchObject] Sketch007
  ArcFitTolerance = 1e-06
  AttachmentSupport = -> [Pad003]
  ExternalGeometry = -> [Pad003]
  ExternalTypes = [0]
  FullyConstrained = true
  MakeInternals = false
  MapMode = 5
  Placement = pos=(53.5,0,0) rot=(0.57735,0.57735,0.57735;2.0944rad)
  sketch-geometry (7):
    g0: GeomPoint X=51.8191 Y=4.2 Z=0
    g1: LineSegment StartX=51.8191 StartY=4.2 StartZ=0 EndX=47.6191 EndY=8.4 EndZ=0
    g2: LineSegment StartX=51.8191 StartY=4.2 StartZ=0 EndX=47.6191 EndY=0 EndZ=0
    g3: LineSegment StartX=47.6191 StartY=0 StartZ=0 EndX=51.8191 EndY=0 EndZ=0
    g4: LineSegment StartX=51.8191 StartY=8.4 StartZ=0 EndX=47.6191 EndY=8.4 EndZ=0
    g5: LineSegment StartX=51.8191 StartY=0 StartZ=0 EndX=51.8191 EndY=4.2 EndZ=0
    g6: LineSegment StartX=51.8191 StartY=4.2 StartZ=0 EndX=51.8191 EndY=8.4 EndZ=0
  constraints (17):
    c: Coincident(g1,g0)
    c: Horizontal(g1,g-3)
    c: Angle(g1,g-3) = 0.785398
    c: PointOnObject(g2,g-1)
    c: Coincident(g2,g0)
    c: Vertical(g2,g1)
    c: Coincident(g3,g2)
    c: Coincident(g3,g-4)
    c: Coincident(g4,g1)
    c: Horizontal(g4)
    c: Coincident(g5,g3)
    c: Coincident(g5,g0)
    c: Vertical(g5)
    c: Coincident(g6,g0)
    c: Coincident(g6,g4)
    c: Vertical(g6)
    c: Equal(g2,g1)
FEATURE [PartDesign::Pocket] Pocket003
  BaseFeature = -> Pad003
  Direction = (-1,0,0)
  Length = 50
  Length2 = 5
  Midplane = true
  Placement = pos=(35,0,0) rot=(0,0,1;0rad)
  Profile = -> Sketch007
  ReferenceAxis = -> Sketch007 [N_Axis]
  Refine = true
  Suppressed = false
  Type = 0
FEATURE [Sketcher::SketchObject] Sketch008
  ArcFitTolerance = 1e-06
  AttachmentSupport = -> [Pocket003]
  ExternalTypes = [0]
  FullyConstrained = true
  MakeInternals = false
  MapMode = 5
  Placement = pos=(35,0,8.4) rot=(0,0,1;0rad)
  sketch-geometry (1):
    g0: Circle CenterX=0 CenterY=0 CenterZ=0 NormalX=0 NormalY=0 NormalZ=1 AngleXU=0 Radius=7.5
  constraints (2):
    c: Diameter(g0) = 15
    c: Coincident(g0,g-1)
FEATURE [PartDesign::Pad] Pad004
  BaseFeature = -> Pocket003
  Direction = (0,0,1)
  Length = 6.85
  Length2 = 10
  Placement = pos=(35,0,0) rot=(0,0,1;0rad)
  Profile = -> Sketch008
  ReferenceAxis = -> Sketch008 [N_Axis]
  Refine = true
  Suppressed = false
  Type = 0
  expr: Length = 7 - variables#Spreadsheet.tollerance / 2
FEATURE [Sketcher::SketchObject] Sketch009
  ArcFitTolerance = 1e-06
  AttachmentSupport = -> [Pad004]
  ExternalGeometry = -> [Pad004]
  ExternalTypes = [0]
  FullyConstrained = true
  MakeInternals = false
  MapMode = 5
  Placement = pos=(35,0,15.25) rot=(0,0,1;0rad)
  expr: Constraints[4] = variables#Spreadsheet.shaft_diam
  sketch-geometry (3):
    g0: Circle CenterX=0 CenterY=0 CenterZ=0 NormalX=0 NormalY=0 NormalZ=1 AngleXU=0 Radius=4.75
    g1: Circle CenterX=0 CenterY=0 CenterZ=0 NormalX=0 NormalY=0 NormalZ=1 AngleXU=0 Radius=7.5
    g2: Circle CenterX=0 CenterY=0 CenterZ=0 NormalX=0 NormalY=0 NormalZ=1 AngleXU=0 Radius=3.9
  constraints (6):
    c: Diameter(g0) = 9.5
    c: Coincident(g0,g-1)
    c: Coincident(g1,g0)
    c: Equal(g1,g-3)
    c: Diameter(g2) = 7.8
    c: Coincident(g2,g0)
FEATURE [PartDesign::Pocket] Pocket004
  BaseFeature = -> Pad004
  Direction = (0,0,-1)
  Length = 1
  Length2 = 5
  Placement = pos=(35,0,0) rot=(0,0,1;0rad)
  Profile = -> Sketch009 [Edge1,Edge2]
  ReferenceAxis = -> Sketch009 [N_Axis]
  Refine = true
  Suppressed = false
  Type = 0
FEATURE [PartDesign::Pad] Pad005
  BaseFeature = -> Pocket004
  Direction = (0,0,1)
  Length = 6
  Length2 = 10
  Placement = pos=(35,0,0) rot=(0,0,1;0rad)
  Profile = -> Sketch009 [Edge3]
  ReferenceAxis = -> Sketch009 [N_Axis]
  Refine = true
  Suppressed = false
  Type = 0
FEATURE [PartDesign::Fillet] Fillet001
  Base = -> Pad005 [Edge534,Edge532,Edge530,Edge537]
  BaseFeature = -> Pad005
  Placement = pos=(35,0,0) rot=(0,0,1;0rad)
  Radius = 0.25
  Refine = true
  SupportTransform = false
  Suppressed = false
  UseAllEdges = false
FEATURE [PartDesign::Fillet] Fillet002
  Base = -> Fillet001 [Edge3]
  BaseFeature = -> Fillet001
  Placement = pos=(35,0,0) rot=(0,0,1;0rad)
  Radius = 8
  Refine = true
  SupportTransform = false
  Suppressed = true
  UseAllEdges = false
FEATURE [Sketcher::SketchObject] Sketch010
  ArcFitTolerance = 1e-06
  AttachmentSupport = -> [Fillet002]
  ExternalTypes = [0]
  FullyConstrained = true
  MakeInternals = false
  MapMode = 5
  Placement = pos=(35,0,0) rot=(1,0,0;3.14159rad)
  sketch-geometry (1):
    g0: Circle CenterX=0 CenterY=0 CenterZ=0 NormalX=0 NormalY=0 NormalZ=1 AngleXU=0 Radius=7.5
  constraints (2):
    c: Diameter(g0) = 15
    c: Coincident(g0,g-1)
FEATURE [PartDesign::Pad] Pad006
  BaseFeature = -> Fillet002
  Direction = (0,0,-1)
  Length = 4.45
  Length2 = 10
  Placement = pos=(35,0,0) rot=(0,0,1;0rad)
  Profile = -> Sketch010
  ReferenceAxis = -> Sketch010 [N_Axis]
  Refine = true
  Suppressed = false
  Type = 0
  expr: Length = 4.6 - variables#Spreadsheet.tollerance / 2
FEATURE [Sketcher::SketchObject] Sketch011
  ArcFitTolerance = 1e-06
  AttachmentSupport = -> [Pad006]
  ExternalGeometry = -> [Pad006]
  ExternalTypes = [0]
  FullyConstrained = true
  MakeInternals = false
  MapMode = 5
  Placement = pos=(35,0,-4.45) rot=(1,0,0;3.14159rad)
  expr: Constraints[0] = variables#Spreadsheet.shaft_diam
  sketch-geometry (3):
    g0: Circle CenterX=0 CenterY=0 CenterZ=0 NormalX=0 NormalY=0 NormalZ=1 AngleXU=0 Radius=3.9
    g1: Circle CenterX=0 CenterY=0 CenterZ=0 NormalX=0 NormalY=0 NormalZ=1 AngleXU=0 Radius=4.75
    g2: Circle CenterX=0 CenterY=0 CenterZ=0 NormalX=0 NormalY=0 NormalZ=1 AngleXU=0 Radius=7.5
  constraints (6):
    c: Diameter(g0) = 7.8
    c: Coincident(g0,g-1)
    c: Diameter(g1) = 9.5
    c: Coincident(g1,g0)
    c: Coincident(g2,g0)
    c: Equal(g2,g-3)
FEATURE [PartDesign::Pocket] Pocket005
  BaseFeature = -> Pad006
  Direction = (0,0,1)
  Length = 1
  Length2 = 5
  Placement = pos=(35,0,0) rot=(0,0,1;0rad)
  Profile = -> Sketch011 [Edge3,Edge2]
  ReferenceAxis = -> Sketch011 [N_Axis]
  Refine = true
  Suppressed = false
  Type = 0
FEATURE [PartDesign::Pad] Pad007
  BaseFeature = -> Pocket005
  Direction = (0,0,-1)
  Length = 6
  Length2 = 10
  Placement = pos=(35,0,0) rot=(0,0,1;0rad)
  Profile = -> Sketch011 [Edge1]
  ReferenceAxis = -> Sketch011 [N_Axis]
  Refine = true
  Suppressed = false
  Type = 0
FEATURE [PartDesign::Fillet] Fillet003
  Base = -> Pad007 [Edge544,Edge547,Edge550,Edge554,Edge541]
  BaseFeature = -> Pad007
  Placement = pos=(35,0,0) rot=(0,0,1;0rad)
  Radius = 0.25
  Refine = true
  SupportTransform = false
  Suppressed = false
  UseAllEdges = false
FEATURE [Part::Part2DObjectPython] ShapeString  # Draft 2D object (typed FeaturePython)
  AttachmentOffset = pos=(-13.5,32,0) rot=(0,0,1;1.5708rad)
  AttachmentSupport = -> [Pocket002]
  FontFile = <userpath>/Downloads/Roboto/Roboto-Black.ttf
  Fuse = false
  Justification = 4
  JustificationReference = 0
  KeepLeftMargin = false
  MakeFace = true
  MapMode = 5
  ObliqueAngle = 0
  Placement = pos=(-13.5,32,8.4) rot=(0,0,1;1.5708rad)
  ScaleToSize = true
  Size = 7
  String = 14906 LR
  Tracking = 0
FEATURE [PartDesign::Pocket] Pocket006
  BaseFeature = -> Pocket002
  Direction = (0,0,-1)
  Length = 2
  Length2 = 5
  Profile = -> ShapeString
  ReferenceAxis = -> ShapeString [N_Axis]
  Refine = true
  Suppressed = false
  Type = 0
FEATURE [Part::Part2DObjectPython] ShapeString001  # Draft 2D object (typed FeaturePython)
  AttachmentOffset = pos=(13.5,32,0) rot=(0,0,-1;1.5708rad)
  AttachmentSupport = -> [Fillet003]
  FontFile = <userpath>/Downloads/Roboto/Roboto-Black.ttf
  Fuse = false
  Justification = 4
  JustificationReference = 0
  KeepLeftMargin = false
  MakeFace = true
  MapMode = 5
  ObliqueAngle = 0
  Placement = pos=(48.5,32,8.4) rot=(0,0,-1;1.5708rad)
  ScaleToSize = true
  Size = 7
  String = Open Claw
  Tracking = 0
  expr: .AttachmentOffset.Base.x = -ShapeString.Placement.Base.x
  expr: .AttachmentOffset.Base.y = ShapeString.Placement.Base.y
  expr: Size = ShapeString.Size
FEATURE [PartDesign::Pocket] Pocket007
  BaseFeature = -> Fillet003
  Direction = (0,0,-1)
  Length = 2
  Length2 = 5
  Placement = pos=(35,0,0) rot=(0,0,1;0rad)
  Profile = -> ShapeString001
  ReferenceAxis = -> ShapeString001 [N_Axis]
  Refine = true
  Suppressed = false
  Type = 0
  expr: Length = Pocket006.Length
FEATURE [Sketcher::SketchObject] Sketch012
  ArcFitTolerance = 1e-06
  AttachmentSupport = -> [Pocket007]
  ExternalTypes = [0]
  FullyConstrained = true
  MakeInternals = false
  MapMode = 5
  Placement = pos=(35,0,21.25) rot=(0,0,1;0rad)
  sketch-geometry (1):
    g0: Circle CenterX=0 CenterY=0 CenterZ=0 NormalX=0 NormalY=0 NormalZ=1 AngleXU=0 Radius=2.25
  constraints (2):
    c: Diameter(g0) = 4.5
    c: Coincident(g0,g-1)
FEATURE [PartDesign::Pocket] Pocket008
  BaseFeature = -> Pocket007
  Direction = (0,0,-1)
  Length = 0
  Length2 = 5
  Placement = pos=(35,0,0) rot=(0,0,1;0rad)
  Profile = -> Sketch012
  ReferenceAxis = -> Sketch012 [N_Axis]
  Refine = true
  Suppressed = false
  Type = 3
  UpToFace = -> Pocket007 [Face324]
FEATURE [PartDesign::Hole] Hole
  BaseFeature = -> Pocket008
  CustomThreadClearance = 0
  Depth = 25
  DepthType = 0
  Diameter = 4.5
  DrillForDepth = false
  DrillPoint = 1
  DrillPointAngle = 118
  HoleCutCountersinkAngle = 90
  HoleCutCustomValues = false
  HoleCutDepth = 0
  HoleCutDiameter = 8.4
  HoleCutType = 2
  ModelThread = false
  Placement = pos=(35,0,0) rot=(0,0,1;0rad)
  Profile = -> Pocket008 [Edge932]
  Refine = true
  Suppressed = false
  Tapered = false
  TaperedAngle = 90
  ThreadClass = 0
  ThreadDepth = 25
  ThreadDepthType = 0
  ThreadDirection = 0
  ThreadFit = 0
  ThreadSize = 0
  ThreadType = 0
  Threaded = false
  UseCustomThreadClearance = false
FEATURE [Sketcher::SketchObject] Sketch013
  ArcFitTolerance = 1e-06
  AttachmentSupport = -> [Pocket006]
  ExternalTypes = [0]
  FullyConstrained = true
  MakeInternals = false
  MapMode = 5
  Placement = pos=(0,0,8.4) rot=(0,0,1;0rad)
  sketch-geometry (1):
    g0: Circle CenterX=0 CenterY=0 CenterZ=0 NormalX=0 NormalY=0 NormalZ=1 AngleXU=0 Radius=2.25
  constraints (2):
    c: Coincident(g0,g-1)
    c: Diameter(g0) = 4.5
FEATURE [PartDesign::Hole] Hole001
  BaseFeature = -> Pocket006
  CustomThreadClearance = 0
  Depth = 185.015
  DepthType = 1
  Diameter = 4.5
  DrillForDepth = false
  DrillPoint = 1
  DrillPointAngle = 118
  HoleCutCountersinkAngle = 90
  HoleCutCustomValues = false
  HoleCutDepth = 0.5
  HoleCutDiameter = 10
  HoleCutType = 2
  ModelThread = false
  Profile = -> Sketch013
  Refine = true
  Suppressed = false
  Tapered = false
  TaperedAngle = 90
  ThreadClass = 0
  ThreadDepth = 185.015
  ThreadDepthType = 0
  ThreadDirection = 0
  ThreadFit = 0
  ThreadSize = 0
  ThreadType = 0
  Threaded = false
  UseCustomThreadClearance = false
FEATURE [Sketcher::SketchObject] Sketch014
  ArcFitTolerance = 1e-06
  AttachmentSupport = -> [XZ_Plane]
  ExternalGeometry = -> [Hole001]
  ExternalTypes = [0]
  FullyConstrained = true
  MakeInternals = false
  MapMode = 5
  Placement = pos=(0,0,0) rot=(1,0,0;1.5708rad)
  sketch-geometry (5):
    g0: ArcOfCircle CenterX=17.5 CenterY=7 CenterZ=0 NormalX=0 NormalY=0 NormalZ=1 AngleXU=0 Radius=1.75 StartAngle=3.14159 EndAngle=6.28319
    g1: LineSegment [constr] StartX=5 StartY=8.4 StartZ=0 EndX=25 EndY=8.4 EndZ=0
    g2: LineSegment StartX=19.25 StartY=7 StartZ=0 EndX=19.25 EndY=8.4 EndZ=0
    g3: LineSegment StartX=15.75 StartY=7 StartZ=0 EndX=15.75 EndY=8.4 EndZ=0
    g4: LineSegment StartX=15.75 StartY=8.4 StartZ=0 EndX=19.25 EndY=8.4 EndZ=0
  constraints (15):
    c: DistanceX(g0) = 17.5  'screwdriver_hole_x'
    c: DistanceY(g0) = 7  'screwdriver_hole_y'
    c: Diameter(g0) = 3.5  'screwdriver_hole_diam'
    c: Distance(g1) = 20
    c: Coincident(g1,g-3)
    c: Horizontal(g1)
    c: PointOnObject(g2,g1)
    c: Vertical(g2)
    c: PointOnObject(g3,g1)
    c: Vertical(g3)
    c: Horizontal(g3,g0)
    c: Tangent(g0,g2) = -1.5708
    c: Coincident(g0,g3)
    c: Coincident(g4,g3)
    c: Coincident(g4,g2)
FEATURE [PartDesign::Pocket] Pocket009
  BaseFeature = -> Hole001
  Direction = (0,1,-2e-16)
  Length = 25
  Length2 = 5
  Midplane = true
  Profile = -> Sketch014
  ReferenceAxis = -> Sketch014 [N_Axis]
  Refine = true
  Suppressed = false
  Type = 0
FEATURE [PartDesign::Body] Body  label="Claw Pincher Powered"
  AllowCompound = false
  Group = -> [InvoluteGear,Sketch,Pad,Sketch001,Pocket,Sketch002,Pocket001,Sketch003,Pad001,Fillet,Sketch004,Pad002,Sketch005,Pocket002,ShapeString,Pocket006,Sketch013,Hole001,Sketch014,Pocket009]
  Origin = -> Origin
  Tip = -> Pocket009
FEATURE [Sketcher::SketchObject] Sketch015
  ArcFitTolerance = 1e-06
  AttachmentSupport = -> [XZ_Plane001]
  ExternalGeometry = -> [Hole]
  ExternalTypes = [0]
  FullyConstrained = true
  MakeInternals = false
  MapMode = 5
  Placement = pos=(0,0,0) rot=(1,0,0;1.5708rad)
  expr: Constraints[0] = Sketch014.Constraints.screwdriver_hole_x
  expr: Constraints[1] = Sketch014.Constraints.screwdriver_hole_y
  expr: Constraints[2] = Sketch014.Constraints.screwdriver_hole_diam
  sketch-geometry (5):
    g0: ArcOfCircle CenterX=17.5 CenterY=7 CenterZ=0 NormalX=0 NormalY=0 NormalZ=1 AngleXU=0 Radius=1.75 StartAngle=3.14159 EndAngle=6.28319
    g1: LineSegment [constr] StartX=27.5 StartY=8.4 StartZ=0 EndX=7.5 EndY=8.4 EndZ=0
    g2: LineSegment StartX=19.25 StartY=7 StartZ=0 EndX=19.25 EndY=8.4 EndZ=0
    g3: LineSegment StartX=15.75 StartY=7 StartZ=0 EndX=15.75 EndY=8.4 EndZ=0
    g4: LineSegment StartX=15.75 StartY=8.4 StartZ=0 EndX=19.25 EndY=8.4 EndZ=0
  constraints (14):
    c: DistanceX(g-1,g0) = 17.5
    c: DistanceY(g-1,g0) = 7
    c: Diameter(g0) = 3.5
    c: Coincident(g1,g-3)
    c: Horizontal(g1)
    c: DistanceX(g1,g1) = 20
    c: PointOnObject(g2,g1)
    c: Vertical(g2)
    c: PointOnObject(g3,g1)
    c: Vertical(g3)
    c: Coincident(g4,g3)
    c: Coincident(g4,g2)
    c: Tangent(g0,g2) = -1.5708
    c: Tangent(g0,g3) = 1.5708
FEATURE [PartDesign::Pocket] Pocket010
  BaseFeature = -> Hole
  Direction = (0,1,-2e-16)
  Length = 25
  Length2 = 5
  Midplane = true
  Placement = pos=(35,0,0) rot=(0,0,1;0rad)
  Profile = -> Sketch015
  ReferenceAxis = -> Sketch015 [N_Axis]
  Refine = true
  Suppressed = false
  Type = 0
  expr: Length = Pocket009.Length
FEATURE [PartDesign::Body] Body001  label="Claw Pincher Passive"
  AllowCompound = false
  Group = -> [InvoluteGear001,Sketch006,Binder,Pad003,Sketch007,Pocket003,Sketch008,Pad004,Sketch009,Pocket004,Pad005,Fillet001,Fillet002,Sketch010,Pad006,Sketch011,Pocket005,Pad007,Fillet003,ShapeString001,Pocket007,Sketch012,Pocket008,Hole,Sketch015,Pocket010]
  Origin = -> Origin001
  Tip = -> Pocket010
FEATURE [App::Point] Origin002  label="Origin"
  Role = Origin
FEATURE [App::Point] Origin003  label="Origin"
  Role = Origin
---- part variables.FCStd = doc fcstd_4303f158f4aa ----
FCSTD DOCUMENT  (FreeCAD 1.1R39747 (Git))
Label: variables
License: All rights reserved
LicenseURL: https://en.wikipedia.org/wiki/All_rights_reserved
objects: Spreadsheet::Sheet×1

FEATURE [Spreadsheet::Sheet] Spreadsheet  label="variables"
  MountType = 0
  ServoType = 0
  cells = A2='Pincher Length (35mm Minimum); B2='Tollerance; C2='Claw Back Spacer Diameter; D2='Claw Back Outer Spacer Holes Wing Angle; E2='Claw Pincher C2C; F2='Claw Base Thickness; G2='Claw Back Spacer Length; H2='3DP Shaft Diam; I2='Claw Spacer Screw Length; J2='Camera Mount Pillar Len; K2='Camera Mount Pillar Thickness; L2='Distance Bearing Holes to End; M2='Claw Short Wall Distance; N2='Camera Mount; O2='Hub Mount Countersink; A3(claw_pincher_length)=35; B3(tollerance)=0.3; C3(claw_back_spacer_diameter)=8; D3(claw_back_outer_spacer_holes_wing_angle)=150; E3(claw_pincher_c2c)=35; F3(claw_base_thickness)=8.7; G3(claw_back_spacer_length)=22; H3(shaft_diam)=7.8; I3(claw_spacer_screw_len)=45; J3(camera_mount_pillar_len)=16; K3(camera_mount_pillar_thickness)=7; L3(distance_bearing_holes_to_end)=16; M3(claw_short_wall_distance)=30; N3(use_camera_mount)=0; O3(Hub_Mount_Countersink)=1; A5='Servo; B5='HolesToSpline; C5='HolesHorizDistance; D5='HolesVertDistance; E5='GobildaSrvVisible; F5='DSServoVisible; A6==hiddenref(.ServoType.String); B6(servo_holes_to_spline)==.B7; C6(servo_holes_horiz_dist)==.C7; D6(servo_holes_vert_dist)==.D7; E6(gobilda_servo_visible)==.E7; F6(dsservo_visible)==.F7; A7='DSServo; B7=14.75; C7=49.5; D7=9.9; E7=0; F7=1; A8='Gobilda; B8=14.2; C8=48; D8=9.9; E8=1; F8=0; A11='Mount Type; B11='Rex Mount; C11='Hub Mount; A12==hiddenref(.MountType.String); B12(rex_mount)==.B13; C12(hub_mount)==.C13; A13='Rex Mount; B13=1; C13=0; A14='Hub Mount; B14=0; C14=1
  expr: .MountType.Enum = cells[<<A13:|>>]
  expr: .ServoType.Enum = cells[<<A7:|>>]
  expr: .cells.Bind.B12.C12 = tuple(.cells; <<B>> + str(hiddenref(MountType) + 13); <<C>> + str(hiddenref(MountType) + 13))
  expr: .cells.Bind.B6.F6 = tuple(.cells; <<B>> + str(hiddenref(ServoType) + 7); <<F>> + str(hiddenref(ServoType) + 7))
